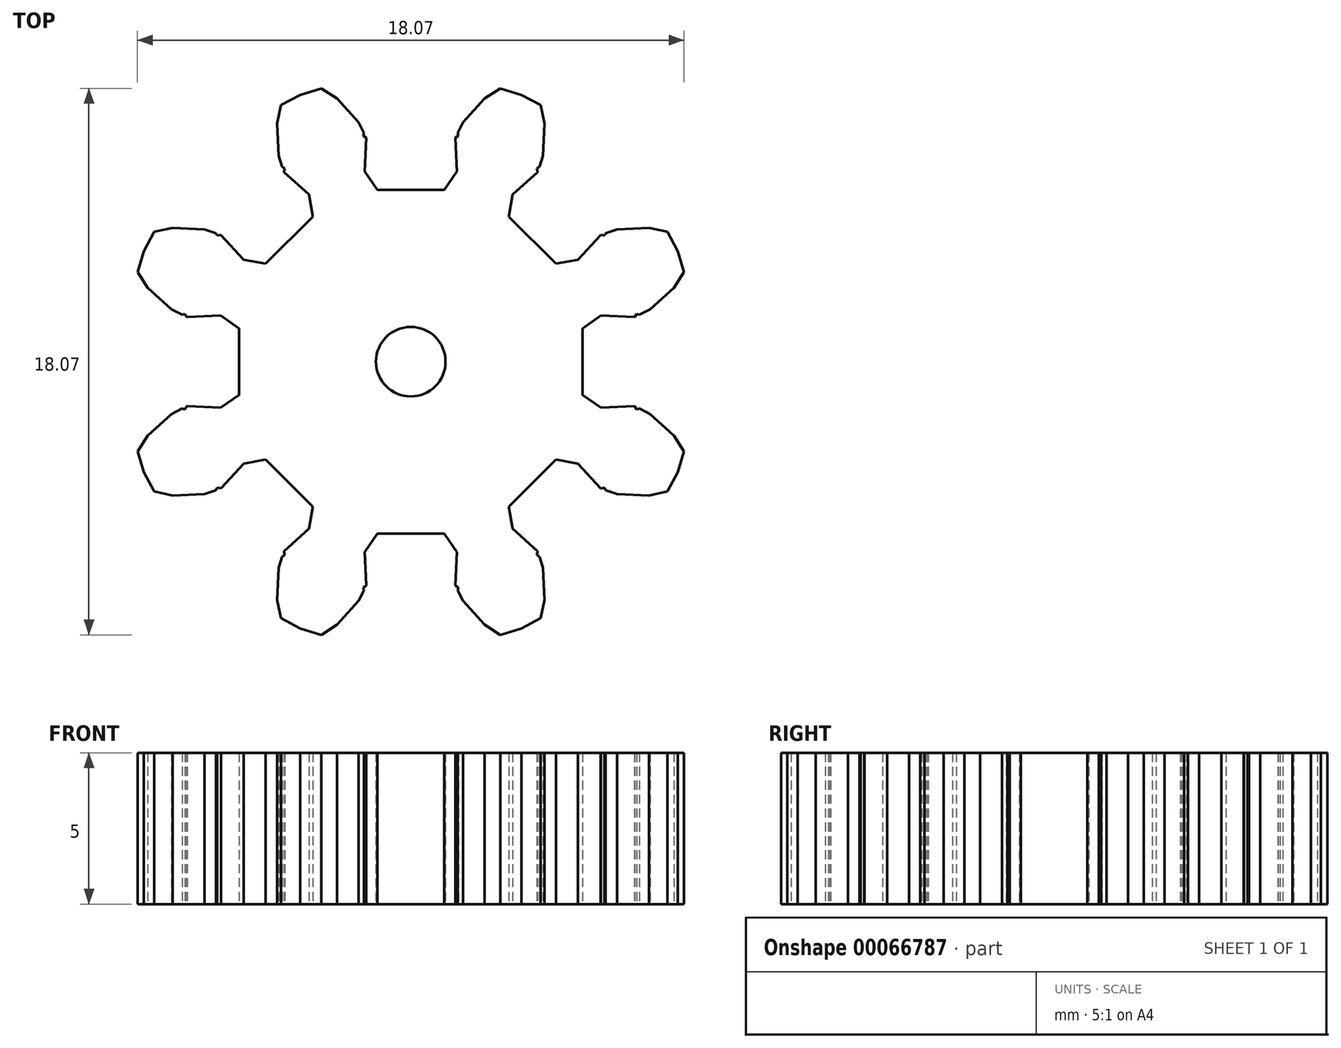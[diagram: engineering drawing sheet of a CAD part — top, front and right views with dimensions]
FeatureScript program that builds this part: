
annotation { "Feature Type Name" : "Feature", "Feature Type Description" : "" }
export const myFeature = defineFeature(function(context is Context, id is Id, definition is map)
    precondition{}
    {
        {
            var Q0;
            Q0=qCreatedBy(makeId("Top.planeOp"),FACE);
            var sketch = newSketch(context, id + "F0", { "sketchPlane" : qUnion([Q0])});
            skLineSegment(sketch, "E0", {"start": v(17.9, -7.29) * mm, "end": v(18.18, -6.43) * mm});
            skLineSegment(sketch, "E1", {"start": v(18.18, -6.43) * mm, "end": v(18.36, -5.54) * mm});
            skLineSegment(sketch, "E2", {"start": v(18.36, -5.54) * mm, "end": v(18.22, -5.43) * mm});
            skLineSegment(sketch, "E3", {"start": v(18.22, -5.43) * mm, "end": v(17.56, -4.97) * mm});
            skLineSegment(sketch, "E4", {"start": v(17.56, -4.97) * mm, "end": v(17, -4.65) * mm});
            skLineSegment(sketch, "E5", {"start": v(17, -4.65) * mm, "end": v(16.58, -4.46) * mm});
            skLineSegment(sketch, "E6", {"start": v(16.58, -4.46) * mm, "end": v(16.3, -4.36) * mm});
            skLineSegment(sketch, "E7", {"start": v(16.3, -4.36) * mm, "end": v(16.21, -4.33) * mm});
            skLineSegment(sketch, "E8", {"start": v(16.21, -4.33) * mm, "end": v(15.9, -4.3) * mm});
            skLineSegment(sketch, "E9", {"start": v(15.9, -4.3) * mm, "end": v(15.36, -4.19) * mm});
            skLineSegment(sketch, "E10", {"start": v(15.36, -4.19) * mm, "end": v(15, -4.02) * mm});
            skLineSegment(sketch, "E11", {"start": v(15, -4.02) * mm, "end": v(14.83, -3.83) * mm});
            skLineSegment(sketch, "E12", {"start": v(14.83, -3.83) * mm, "end": v(14.86, -3.66) * mm});
            skLineSegment(sketch, "E13", {"start": v(14.86, -3.66) * mm, "end": v(14.86, -3.65) * mm});
            skLineSegment(sketch, "E14", {"start": v(14.86, -3.65) * mm, "end": v(15.1, -1.83) * mm});
            skLineSegment(sketch, "E15", {"start": v(15.1, -1.83) * mm, "end": v(15.1, -1.82) * mm});
            skLineSegment(sketch, "E16", {"start": v(15.1, -1.82) * mm, "end": v(15.12, -1.65) * mm});
            skLineSegment(sketch, "E17", {"start": v(15.12, -1.65) * mm, "end": v(15.33, -1.51) * mm});
            skLineSegment(sketch, "E18", {"start": v(15.33, -1.51) * mm, "end": v(15.72, -1.44) * mm});
            skLineSegment(sketch, "E19", {"start": v(15.72, -1.44) * mm, "end": v(16.28, -1.46) * mm});
            skLineSegment(sketch, "E20", {"start": v(16.28, -1.46) * mm, "end": v(16.58, -1.52) * mm});
            skLineSegment(sketch, "E21", {"start": v(16.58, -1.52) * mm, "end": v(16.68, -1.52) * mm});
            skLineSegment(sketch, "E22", {"start": v(16.68, -1.52) * mm, "end": v(16.97, -1.5) * mm});
            skLineSegment(sketch, "E23", {"start": v(16.97, -1.5) * mm, "end": v(17.43, -1.42) * mm});
            skLineSegment(sketch, "E24", {"start": v(17.43, -1.42) * mm, "end": v(18.04, -1.26) * mm});
            skLineSegment(sketch, "E25", {"start": v(18.04, -1.26) * mm, "end": v(18.8, -0.98) * mm});
            skLineSegment(sketch, "E26", {"start": v(18.8, -0.98) * mm, "end": v(18.97, -0.9) * mm});
            skLineSegment(sketch, "E27", {"start": v(18.97, -0.9) * mm, "end": v(19.03, 0) * mm});
            skLineSegment(sketch, "E28", {"start": v(19.03, 0) * mm, "end": v(18.97, 0.9) * mm});
            skLineSegment(sketch, "E29", {"start": v(18.97, 0.9) * mm, "end": v(18.8, 0.98) * mm});
            skLineSegment(sketch, "E30", {"start": v(18.8, 0.98) * mm, "end": v(18.04, 1.25) * mm});
            skLineSegment(sketch, "E31", {"start": v(18.04, 1.25) * mm, "end": v(17.43, 1.4) * mm});
            skLineSegment(sketch, "E32", {"start": v(17.43, 1.4) * mm, "end": v(16.97, 1.49) * mm});
            skLineSegment(sketch, "E33", {"start": v(16.97, 1.49) * mm, "end": v(16.68, 1.51) * mm});
            skLineSegment(sketch, "E34", {"start": v(16.68, 1.51) * mm, "end": v(16.58, 1.51) * mm});
            skLineSegment(sketch, "E35", {"start": v(16.58, 1.51) * mm, "end": v(16.28, 1.46) * mm});
            skLineSegment(sketch, "E36", {"start": v(16.28, 1.46) * mm, "end": v(15.72, 1.43) * mm});
            skLineSegment(sketch, "E37", {"start": v(15.72, 1.43) * mm, "end": v(15.33, 1.5) * mm});
            skLineSegment(sketch, "E38", {"start": v(15.33, 1.5) * mm, "end": v(15.12, 1.64) * mm});
            skLineSegment(sketch, "E39", {"start": v(15.12, 1.64) * mm, "end": v(15.1, 1.8) * mm});
            skLineSegment(sketch, "E40", {"start": v(15.1, 1.8) * mm, "end": v(15.1, 1.82) * mm});
            skLineSegment(sketch, "E41", {"start": v(15.1, 1.82) * mm, "end": v(14.86, 3.64) * mm});
            skLineSegment(sketch, "E42", {"start": v(14.86, 3.64) * mm, "end": v(14.86, 3.65) * mm});
            skLineSegment(sketch, "E43", {"start": v(14.86, 3.65) * mm, "end": v(14.83, 3.82) * mm});
            skLineSegment(sketch, "E44", {"start": v(14.83, 3.82) * mm, "end": v(15, 4) * mm});
            skLineSegment(sketch, "E45", {"start": v(15, 4) * mm, "end": v(15.36, 4.18) * mm});
            skLineSegment(sketch, "E46", {"start": v(15.36, 4.18) * mm, "end": v(15.9, 4.3) * mm});
            skLineSegment(sketch, "E47", {"start": v(15.9, 4.3) * mm, "end": v(16.21, 4.33) * mm});
            skLineSegment(sketch, "E48", {"start": v(16.21, 4.33) * mm, "end": v(16.3, 4.35) * mm});
            skLineSegment(sketch, "E49", {"start": v(16.3, 4.35) * mm, "end": v(16.58, 4.45) * mm});
            skLineSegment(sketch, "E50", {"start": v(16.58, 4.45) * mm, "end": v(17, 4.64) * mm});
            skLineSegment(sketch, "E51", {"start": v(17, 4.64) * mm, "end": v(17.56, 4.96) * mm});
            skLineSegment(sketch, "E52", {"start": v(17.56, 4.96) * mm, "end": v(18.22, 5.42) * mm});
            skLineSegment(sketch, "E53", {"start": v(18.22, 5.42) * mm, "end": v(18.36, 5.53) * mm});
            skLineSegment(sketch, "E54", {"start": v(18.36, 5.53) * mm, "end": v(18.18, 6.42) * mm});
            skLineSegment(sketch, "E55", {"start": v(18.18, 6.42) * mm, "end": v(17.9, 7.28) * mm});
            skLineSegment(sketch, "E56", {"start": v(17.9, 7.28) * mm, "end": v(17.71, 7.31) * mm});
            skLineSegment(sketch, "E57", {"start": v(17.71, 7.31) * mm, "end": v(16.9, 7.38) * mm});
            skLineSegment(sketch, "E58", {"start": v(16.9, 7.38) * mm, "end": v(16.27, 7.37) * mm});
            skLineSegment(sketch, "E59", {"start": v(16.27, 7.37) * mm, "end": v(15.81, 7.33) * mm});
            skLineSegment(sketch, "E60", {"start": v(15.81, 7.33) * mm, "end": v(15.52, 7.28) * mm});
            skLineSegment(sketch, "E61", {"start": v(15.52, 7.28) * mm, "end": v(15.43, 7.25) * mm});
            skLineSegment(sketch, "E62", {"start": v(15.43, 7.25) * mm, "end": v(15.15, 7.12) * mm});
            skLineSegment(sketch, "E63", {"start": v(15.15, 7.12) * mm, "end": v(14.62, 6.95) * mm});
            skLineSegment(sketch, "E64", {"start": v(14.62, 6.95) * mm, "end": v(14.22, 6.92) * mm});
            skLineSegment(sketch, "E65", {"start": v(14.22, 6.92) * mm, "end": v(13.98, 7) * mm});
            skLineSegment(sketch, "E66", {"start": v(13.98, 7) * mm, "end": v(13.92, 7.16) * mm});
            skLineSegment(sketch, "E67", {"start": v(13.92, 7.16) * mm, "end": v(13.91, 7.17) * mm});
            skLineSegment(sketch, "E68", {"start": v(13.91, 7.17) * mm, "end": v(13.21, 8.86) * mm});
            skLineSegment(sketch, "E69", {"start": v(13.21, 8.86) * mm, "end": v(13.2, 8.88) * mm});
            skLineSegment(sketch, "E70", {"start": v(13.2, 8.88) * mm, "end": v(13.14, 9.03) * mm});
            skLineSegment(sketch, "E71", {"start": v(13.14, 9.03) * mm, "end": v(13.25, 9.26) * mm});
            skLineSegment(sketch, "E72", {"start": v(13.25, 9.26) * mm, "end": v(13.56, 9.51) * mm});
            skLineSegment(sketch, "E73", {"start": v(13.56, 9.51) * mm, "end": v(14.05, 9.77) * mm});
            skLineSegment(sketch, "E74", {"start": v(14.05, 9.77) * mm, "end": v(14.34, 9.88) * mm});
            skLineSegment(sketch, "E75", {"start": v(14.34, 9.88) * mm, "end": v(14.43, 9.92) * mm});
            skLineSegment(sketch, "E76", {"start": v(14.43, 9.92) * mm, "end": v(14.67, 10.1) * mm});
            skLineSegment(sketch, "E77", {"start": v(14.67, 10.1) * mm, "end": v(15.02, 10.39) * mm});
            skLineSegment(sketch, "E78", {"start": v(15.02, 10.39) * mm, "end": v(15.48, 10.83) * mm});
            skLineSegment(sketch, "E79", {"start": v(15.48, 10.83) * mm, "end": v(16, 11.45) * mm});
            skLineSegment(sketch, "E80", {"start": v(16, 11.45) * mm, "end": v(16.1, 11.6) * mm});
            skLineSegment(sketch, "E81", {"start": v(16.1, 11.6) * mm, "end": v(15.7, 12.41) * mm});
            skLineSegment(sketch, "E82", {"start": v(15.7, 12.41) * mm, "end": v(15.2, 13.16) * mm});
            skLineSegment(sketch, "E83", {"start": v(15.2, 13.16) * mm, "end": v(15.02, 13.15) * mm});
            skLineSegment(sketch, "E84", {"start": v(15.02, 13.15) * mm, "end": v(14.22, 13) * mm});
            skLineSegment(sketch, "E85", {"start": v(14.22, 13) * mm, "end": v(13.61, 12.84) * mm});
            skLineSegment(sketch, "E86", {"start": v(13.61, 12.84) * mm, "end": v(13.18, 12.67) * mm});
            skLineSegment(sketch, "E87", {"start": v(13.18, 12.67) * mm, "end": v(12.91, 12.55) * mm});
            skLineSegment(sketch, "E88", {"start": v(12.91, 12.55) * mm, "end": v(12.83, 12.5) * mm});
            skLineSegment(sketch, "E89", {"start": v(12.83, 12.5) * mm, "end": v(12.6, 12.3) * mm});
            skLineSegment(sketch, "E90", {"start": v(12.6, 12.3) * mm, "end": v(12.12, 12) * mm});
            skLineSegment(sketch, "E91", {"start": v(12.12, 12) * mm, "end": v(11.75, 11.87) * mm});
            skLineSegment(sketch, "E92", {"start": v(11.75, 11.87) * mm, "end": v(11.5, 11.88) * mm});
            skLineSegment(sketch, "E93", {"start": v(11.5, 11.88) * mm, "end": v(11.4, 12.01) * mm});
            skLineSegment(sketch, "E94", {"start": v(11.4, 12.01) * mm, "end": v(11.38, 12.03) * mm});
            skLineSegment(sketch, "E95", {"start": v(11.38, 12.03) * mm, "end": v(10.27, 13.48) * mm});
            skLineSegment(sketch, "E96", {"start": v(10.27, 13.48) * mm, "end": v(10.26, 13.5) * mm});
            skLineSegment(sketch, "E97", {"start": v(10.26, 13.5) * mm, "end": v(10.16, 13.63) * mm});
            skLineSegment(sketch, "E98", {"start": v(10.16, 13.63) * mm, "end": v(10.2, 13.87) * mm});
            skLineSegment(sketch, "E99", {"start": v(10.2, 13.87) * mm, "end": v(10.43, 14.2) * mm});
            skLineSegment(sketch, "E100", {"start": v(10.43, 14.2) * mm, "end": v(10.84, 14.58) * mm});
            skLineSegment(sketch, "E101", {"start": v(10.84, 14.58) * mm, "end": v(11.1, 14.75) * mm});
            skLineSegment(sketch, "E102", {"start": v(11.1, 14.75) * mm, "end": v(11.17, 14.82) * mm});
            skLineSegment(sketch, "E103", {"start": v(11.17, 14.82) * mm, "end": v(11.36, 15.05) * mm});
            skLineSegment(sketch, "E104", {"start": v(11.36, 15.05) * mm, "end": v(11.63, 15.42) * mm});
            skLineSegment(sketch, "E105", {"start": v(11.63, 15.42) * mm, "end": v(11.95, 15.97) * mm});
            skLineSegment(sketch, "E106", {"start": v(11.95, 15.97) * mm, "end": v(12.29, 16.7) * mm});
            skLineSegment(sketch, "E107", {"start": v(12.29, 16.7) * mm, "end": v(12.35, 16.87) * mm});
            skLineSegment(sketch, "E108", {"start": v(12.35, 16.87) * mm, "end": v(11.76, 17.55) * mm});
            skLineSegment(sketch, "E109", {"start": v(11.76, 17.55) * mm, "end": v(11.07, 18.15) * mm});
            skLineSegment(sketch, "E110", {"start": v(11.07, 18.15) * mm, "end": v(10.9, 18.09) * mm});
            skLineSegment(sketch, "E111", {"start": v(10.9, 18.09) * mm, "end": v(10.17, 17.74) * mm});
            skLineSegment(sketch, "E112", {"start": v(10.17, 17.74) * mm, "end": v(9.63, 17.42) * mm});
            skLineSegment(sketch, "E113", {"start": v(9.63, 17.42) * mm, "end": v(9.25, 17.15) * mm});
            skLineSegment(sketch, "E114", {"start": v(9.25, 17.15) * mm, "end": v(9.02, 16.96) * mm});
            skLineSegment(sketch, "E115", {"start": v(9.02, 16.96) * mm, "end": v(8.96, 16.9) * mm});
            skLineSegment(sketch, "E116", {"start": v(8.96, 16.9) * mm, "end": v(8.78, 16.64) * mm});
            skLineSegment(sketch, "E117", {"start": v(8.78, 16.64) * mm, "end": v(8.4, 16.23) * mm});
            skLineSegment(sketch, "E118", {"start": v(8.4, 16.23) * mm, "end": v(8.08, 16) * mm});
            skLineSegment(sketch, "E119", {"start": v(8.08, 16) * mm, "end": v(7.83, 15.95) * mm});
            skLineSegment(sketch, "E120", {"start": v(7.83, 15.95) * mm, "end": v(7.7, 16.06) * mm});
            skLineSegment(sketch, "E121", {"start": v(7.7, 16.06) * mm, "end": v(7.68, 16.07) * mm});
            skLineSegment(sketch, "E122", {"start": v(7.68, 16.07) * mm, "end": v(6.23, 17.18) * mm});
            skLineSegment(sketch, "E123", {"start": v(6.23, 17.18) * mm, "end": v(6.22, 17.19) * mm});
            skLineSegment(sketch, "E124", {"start": v(6.22, 17.19) * mm, "end": v(6.08, 17.3) * mm});
            skLineSegment(sketch, "E125", {"start": v(6.08, 17.3) * mm, "end": v(6.07, 17.54) * mm});
            skLineSegment(sketch, "E126", {"start": v(6.07, 17.54) * mm, "end": v(6.2, 17.92) * mm});
            skLineSegment(sketch, "E127", {"start": v(6.2, 17.92) * mm, "end": v(6.5, 18.39) * mm});
            skLineSegment(sketch, "E128", {"start": v(6.5, 18.39) * mm, "end": v(6.7, 18.62) * mm});
            skLineSegment(sketch, "E129", {"start": v(6.7, 18.62) * mm, "end": v(6.75, 18.7) * mm});
            skLineSegment(sketch, "E130", {"start": v(6.75, 18.7) * mm, "end": v(6.88, 18.97) * mm});
            skLineSegment(sketch, "E131", {"start": v(6.88, 18.97) * mm, "end": v(7.04, 19.4) * mm});
            skLineSegment(sketch, "E132", {"start": v(7.04, 19.4) * mm, "end": v(7.2, 20.02) * mm});
            skLineSegment(sketch, "E133", {"start": v(7.2, 20.02) * mm, "end": v(7.35, 20.81) * mm});
            skLineSegment(sketch, "E134", {"start": v(7.35, 20.81) * mm, "end": v(7.37, 21) * mm});
            skLineSegment(sketch, "E135", {"start": v(7.37, 21) * mm, "end": v(6.61, 21.5) * mm});
            skLineSegment(sketch, "E136", {"start": v(6.61, 21.5) * mm, "end": v(5.8, 21.9) * mm});
            skLineSegment(sketch, "E137", {"start": v(5.8, 21.9) * mm, "end": v(5.65, 21.8) * mm});
            skLineSegment(sketch, "E138", {"start": v(5.65, 21.8) * mm, "end": v(5.04, 21.27) * mm});
            skLineSegment(sketch, "E139", {"start": v(5.04, 21.27) * mm, "end": v(4.6, 20.82) * mm});
            skLineSegment(sketch, "E140", {"start": v(4.6, 20.82) * mm, "end": v(4.3, 20.46) * mm});
            skLineSegment(sketch, "E141", {"start": v(4.3, 20.46) * mm, "end": v(4.13, 20.22) * mm});
            skLineSegment(sketch, "E142", {"start": v(4.13, 20.22) * mm, "end": v(4.08, 20.14) * mm});
            skLineSegment(sketch, "E143", {"start": v(4.08, 20.14) * mm, "end": v(3.98, 19.85) * mm});
            skLineSegment(sketch, "E144", {"start": v(3.98, 19.85) * mm, "end": v(3.72, 19.35) * mm});
            skLineSegment(sketch, "E145", {"start": v(3.72, 19.35) * mm, "end": v(3.46, 19.05) * mm});
            skLineSegment(sketch, "E146", {"start": v(3.46, 19.05) * mm, "end": v(3.24, 18.94) * mm});
            skLineSegment(sketch, "E147", {"start": v(3.24, 18.94) * mm, "end": v(3.08, 19) * mm});
            skLineSegment(sketch, "E148", {"start": v(3.08, 19) * mm, "end": v(3.06, 19) * mm});
            skLineSegment(sketch, "E149", {"start": v(3.06, 19) * mm, "end": v(1.37, 19.7) * mm});
            skLineSegment(sketch, "E150", {"start": v(1.37, 19.7) * mm, "end": v(1.36, 19.71) * mm});
            skLineSegment(sketch, "E151", {"start": v(1.36, 19.71) * mm, "end": v(1.2, 19.78) * mm});
            skLineSegment(sketch, "E152", {"start": v(1.2, 19.78) * mm, "end": v(1.13, 20.02) * mm});
            skLineSegment(sketch, "E153", {"start": v(1.13, 20.02) * mm, "end": v(1.16, 20.41) * mm});
            skLineSegment(sketch, "E154", {"start": v(1.16, 20.41) * mm, "end": v(1.32, 20.95) * mm});
            skLineSegment(sketch, "E155", {"start": v(1.32, 20.95) * mm, "end": v(1.46, 21.23) * mm});
            skLineSegment(sketch, "E156", {"start": v(1.46, 21.23) * mm, "end": v(1.48, 21.32) * mm});
            skLineSegment(sketch, "E157", {"start": v(1.48, 21.32) * mm, "end": v(1.53, 21.6) * mm});
            skLineSegment(sketch, "E158", {"start": v(1.53, 21.6) * mm, "end": v(1.58, 22.07) * mm});
            skLineSegment(sketch, "E159", {"start": v(1.58, 22.07) * mm, "end": v(1.58, 22.7) * mm});
            skLineSegment(sketch, "E160", {"start": v(1.58, 22.7) * mm, "end": v(1.51, 23.5) * mm});
            skLineSegment(sketch, "E161", {"start": v(1.51, 23.5) * mm, "end": v(1.48, 23.69) * mm});
            skLineSegment(sketch, "E162", {"start": v(1.48, 23.69) * mm, "end": v(0.62, 23.98) * mm});
            skLineSegment(sketch, "E163", {"start": v(0.62, 23.98) * mm, "end": v(-0.26, 24.15) * mm});
            skLineSegment(sketch, "E164", {"start": v(-0.26, 24.15) * mm, "end": v(-0.38, 24.01) * mm});
            skLineSegment(sketch, "E165", {"start": v(-0.38, 24.01) * mm, "end": v(-0.84, 23.35) * mm});
            skLineSegment(sketch, "E166", {"start": v(-0.84, 23.35) * mm, "end": v(-1.15, 22.8) * mm});
            skLineSegment(sketch, "E167", {"start": v(-1.15, 22.8) * mm, "end": v(-1.35, 22.38) * mm});
            skLineSegment(sketch, "E168", {"start": v(-1.35, 22.38) * mm, "end": v(-1.45, 22.1) * mm});
            skLineSegment(sketch, "E169", {"start": v(-1.45, 22.1) * mm, "end": v(-1.47, 22) * mm});
            skLineSegment(sketch, "E170", {"start": v(-1.47, 22) * mm, "end": v(-1.5, 21.7) * mm});
            skLineSegment(sketch, "E171", {"start": v(-1.5, 21.7) * mm, "end": v(-1.62, 21.16) * mm});
            skLineSegment(sketch, "E172", {"start": v(-1.62, 21.16) * mm, "end": v(-1.79, 20.8) * mm});
            skLineSegment(sketch, "E173", {"start": v(-1.79, 20.8) * mm, "end": v(-1.97, 20.63) * mm});
            skLineSegment(sketch, "E174", {"start": v(-1.97, 20.63) * mm, "end": v(-2.14, 20.65) * mm});
            skLineSegment(sketch, "E175", {"start": v(-2.14, 20.65) * mm, "end": v(-2.16, 20.66) * mm});
            skLineSegment(sketch, "E176", {"start": v(-2.16, 20.66) * mm, "end": v(-3.97, 20.9) * mm});
            skLineSegment(sketch, "E177", {"start": v(-3.97, 20.9) * mm, "end": v(-3.99, 20.9) * mm});
            skLineSegment(sketch, "E178", {"start": v(-3.99, 20.9) * mm, "end": v(-4.16, 20.92) * mm});
            skLineSegment(sketch, "E179", {"start": v(-4.16, 20.92) * mm, "end": v(-4.3, 21.13) * mm});
            skLineSegment(sketch, "E180", {"start": v(-4.3, 21.13) * mm, "end": v(-4.36, 21.52) * mm});
            skLineSegment(sketch, "E181", {"start": v(-4.36, 21.52) * mm, "end": v(-4.34, 22.08) * mm});
            skLineSegment(sketch, "E182", {"start": v(-4.34, 22.08) * mm, "end": v(-4.29, 22.38) * mm});
            skLineSegment(sketch, "E183", {"start": v(-4.29, 22.38) * mm, "end": v(-4.29, 22.48) * mm});
            skLineSegment(sketch, "E184", {"start": v(-4.29, 22.48) * mm, "end": v(-4.3, 22.77) * mm});
            skLineSegment(sketch, "E185", {"start": v(-4.3, 22.77) * mm, "end": v(-4.39, 23.23) * mm});
            skLineSegment(sketch, "E186", {"start": v(-4.39, 23.23) * mm, "end": v(-4.55, 23.84) * mm});
            skLineSegment(sketch, "E187", {"start": v(-4.55, 23.84) * mm, "end": v(-4.82, 24.6) * mm});
            skLineSegment(sketch, "E188", {"start": v(-4.82, 24.6) * mm, "end": v(-4.9, 24.76) * mm});
            skLineSegment(sketch, "E189", {"start": v(-4.9, 24.76) * mm, "end": v(-5.8, 24.82) * mm});
            skLineSegment(sketch, "E190", {"start": v(-5.8, 24.82) * mm, "end": v(-6.7, 24.76) * mm});
            skLineSegment(sketch, "E191", {"start": v(-6.7, 24.76) * mm, "end": v(-6.78, 24.6) * mm});
            skLineSegment(sketch, "E192", {"start": v(-6.78, 24.6) * mm, "end": v(-7.05, 23.84) * mm});
            skLineSegment(sketch, "E193", {"start": v(-7.05, 23.84) * mm, "end": v(-7.21, 23.23) * mm});
            skLineSegment(sketch, "E194", {"start": v(-7.21, 23.23) * mm, "end": v(-7.3, 22.77) * mm});
            skLineSegment(sketch, "E195", {"start": v(-7.3, 22.77) * mm, "end": v(-7.32, 22.48) * mm});
            skLineSegment(sketch, "E196", {"start": v(-7.32, 22.48) * mm, "end": v(-7.32, 22.38) * mm});
            skLineSegment(sketch, "E197", {"start": v(-7.32, 22.38) * mm, "end": v(-7.26, 22.08) * mm});
            skLineSegment(sketch, "E198", {"start": v(-7.26, 22.08) * mm, "end": v(-7.24, 21.52) * mm});
            skLineSegment(sketch, "E199", {"start": v(-7.24, 21.52) * mm, "end": v(-7.3, 21.13) * mm});
            skLineSegment(sketch, "E200", {"start": v(-7.3, 21.13) * mm, "end": v(-7.44, 20.92) * mm});
            skLineSegment(sketch, "E201", {"start": v(-7.44, 20.92) * mm, "end": v(-7.61, 20.9) * mm});
            skLineSegment(sketch, "E202", {"start": v(-7.61, 20.9) * mm, "end": v(-7.63, 20.9) * mm});
            skLineSegment(sketch, "E203", {"start": v(-7.63, 20.9) * mm, "end": v(-9.44, 20.66) * mm});
            skLineSegment(sketch, "E204", {"start": v(-9.44, 20.66) * mm, "end": v(-9.46, 20.65) * mm});
            skLineSegment(sketch, "E205", {"start": v(-9.46, 20.65) * mm, "end": v(-9.63, 20.63) * mm});
            skLineSegment(sketch, "E206", {"start": v(-9.63, 20.63) * mm, "end": v(-9.81, 20.8) * mm});
            skLineSegment(sketch, "E207", {"start": v(-9.81, 20.8) * mm, "end": v(-9.98, 21.16) * mm});
            skLineSegment(sketch, "E208", {"start": v(-9.98, 21.16) * mm, "end": v(-10.1, 21.7) * mm});
            skLineSegment(sketch, "E209", {"start": v(-10.1, 21.7) * mm, "end": v(-10.13, 22) * mm});
            skLineSegment(sketch, "E210", {"start": v(-10.13, 22) * mm, "end": v(-10.16, 22.1) * mm});
            skLineSegment(sketch, "E211", {"start": v(-10.16, 22.1) * mm, "end": v(-10.26, 22.38) * mm});
            skLineSegment(sketch, "E212", {"start": v(-10.26, 22.38) * mm, "end": v(-10.45, 22.8) * mm});
            skLineSegment(sketch, "E213", {"start": v(-10.45, 22.8) * mm, "end": v(-10.76, 23.35) * mm});
            skLineSegment(sketch, "E214", {"start": v(-10.76, 23.35) * mm, "end": v(-11.22, 24.01) * mm});
            skLineSegment(sketch, "E215", {"start": v(-11.22, 24.01) * mm, "end": v(-11.34, 24.15) * mm});
            skLineSegment(sketch, "E216", {"start": v(-11.34, 24.15) * mm, "end": v(-12.23, 23.98) * mm});
            skLineSegment(sketch, "E217", {"start": v(-12.23, 23.98) * mm, "end": v(-13.08, 23.69) * mm});
            skLineSegment(sketch, "E218", {"start": v(-13.08, 23.69) * mm, "end": v(-13.12, 23.5) * mm});
            skLineSegment(sketch, "E219", {"start": v(-13.12, 23.5) * mm, "end": v(-13.18, 22.7) * mm});
            skLineSegment(sketch, "E220", {"start": v(-13.18, 22.7) * mm, "end": v(-13.18, 22.07) * mm});
            skLineSegment(sketch, "E221", {"start": v(-13.18, 22.07) * mm, "end": v(-13.14, 21.6) * mm});
            skLineSegment(sketch, "E222", {"start": v(-13.14, 21.6) * mm, "end": v(-13.08, 21.32) * mm});
            skLineSegment(sketch, "E223", {"start": v(-13.08, 21.32) * mm, "end": v(-13.06, 21.23) * mm});
            skLineSegment(sketch, "E224", {"start": v(-13.06, 21.23) * mm, "end": v(-12.93, 20.95) * mm});
            skLineSegment(sketch, "E225", {"start": v(-12.93, 20.95) * mm, "end": v(-12.76, 20.41) * mm});
            skLineSegment(sketch, "E226", {"start": v(-12.76, 20.41) * mm, "end": v(-12.73, 20.02) * mm});
            skLineSegment(sketch, "E227", {"start": v(-12.73, 20.02) * mm, "end": v(-12.8, 19.78) * mm});
            skLineSegment(sketch, "E228", {"start": v(-12.8, 19.78) * mm, "end": v(-12.96, 19.71) * mm});
            skLineSegment(sketch, "E229", {"start": v(-12.96, 19.71) * mm, "end": v(-12.98, 19.7) * mm});
            skLineSegment(sketch, "E230", {"start": v(-12.98, 19.7) * mm, "end": v(-14.67, 19) * mm});
            skLineSegment(sketch, "E231", {"start": v(-14.67, 19) * mm, "end": v(-14.68, 19) * mm});
            skLineSegment(sketch, "E232", {"start": v(-14.68, 19) * mm, "end": v(-14.84, 18.94) * mm});
            skLineSegment(sketch, "E233", {"start": v(-14.84, 18.94) * mm, "end": v(-15.06, 19.05) * mm});
            skLineSegment(sketch, "E234", {"start": v(-15.06, 19.05) * mm, "end": v(-15.32, 19.35) * mm});
            skLineSegment(sketch, "E235", {"start": v(-15.32, 19.35) * mm, "end": v(-15.58, 19.85) * mm});
            skLineSegment(sketch, "E236", {"start": v(-15.58, 19.85) * mm, "end": v(-15.68, 20.14) * mm});
            skLineSegment(sketch, "E237", {"start": v(-15.68, 20.14) * mm, "end": v(-15.73, 20.22) * mm});
            skLineSegment(sketch, "E238", {"start": v(-15.73, 20.22) * mm, "end": v(-15.9, 20.46) * mm});
            skLineSegment(sketch, "E239", {"start": v(-15.9, 20.46) * mm, "end": v(-16.2, 20.82) * mm});
            skLineSegment(sketch, "E240", {"start": v(-16.2, 20.82) * mm, "end": v(-16.64, 21.27) * mm});
            skLineSegment(sketch, "E241", {"start": v(-16.64, 21.27) * mm, "end": v(-17.25, 21.8) * mm});
            skLineSegment(sketch, "E242", {"start": v(-17.25, 21.8) * mm, "end": v(-17.4, 21.9) * mm});
            skLineSegment(sketch, "E243", {"start": v(-17.4, 21.9) * mm, "end": v(-18.22, 21.5) * mm});
            skLineSegment(sketch, "E244", {"start": v(-18.22, 21.5) * mm, "end": v(-18.97, 21) * mm});
            skLineSegment(sketch, "E245", {"start": v(-18.97, 21) * mm, "end": v(-18.95, 20.81) * mm});
            skLineSegment(sketch, "E246", {"start": v(-18.95, 20.81) * mm, "end": v(-18.8, 20.02) * mm});
            skLineSegment(sketch, "E247", {"start": v(-18.8, 20.02) * mm, "end": v(-18.64, 19.4) * mm});
            skLineSegment(sketch, "E248", {"start": v(-18.64, 19.4) * mm, "end": v(-18.48, 18.97) * mm});
            skLineSegment(sketch, "E249", {"start": v(-18.48, 18.97) * mm, "end": v(-18.35, 18.7) * mm});
            skLineSegment(sketch, "E250", {"start": v(-18.35, 18.7) * mm, "end": v(-18.3, 18.62) * mm});
            skLineSegment(sketch, "E251", {"start": v(-18.3, 18.62) * mm, "end": v(-18.1, 18.39) * mm});
            skLineSegment(sketch, "E252", {"start": v(-18.1, 18.39) * mm, "end": v(-17.8, 17.92) * mm});
            skLineSegment(sketch, "E253", {"start": v(-17.8, 17.92) * mm, "end": v(-17.67, 17.54) * mm});
            skLineSegment(sketch, "E254", {"start": v(-17.67, 17.54) * mm, "end": v(-17.69, 17.3) * mm});
            skLineSegment(sketch, "E255", {"start": v(-17.69, 17.3) * mm, "end": v(-17.82, 17.19) * mm});
            skLineSegment(sketch, "E256", {"start": v(-17.82, 17.19) * mm, "end": v(-17.83, 17.18) * mm});
            skLineSegment(sketch, "E257", {"start": v(-17.83, 17.18) * mm, "end": v(-19.29, 16.07) * mm});
            skLineSegment(sketch, "E258", {"start": v(-19.29, 16.07) * mm, "end": v(-19.3, 16.06) * mm});
            skLineSegment(sketch, "E259", {"start": v(-19.3, 16.06) * mm, "end": v(-19.43, 15.95) * mm});
            skLineSegment(sketch, "E260", {"start": v(-19.43, 15.95) * mm, "end": v(-19.68, 16) * mm});
            skLineSegment(sketch, "E261", {"start": v(-19.68, 16) * mm, "end": v(-20, 16.23) * mm});
            skLineSegment(sketch, "E262", {"start": v(-20, 16.23) * mm, "end": v(-20.38, 16.64) * mm});
            skLineSegment(sketch, "E263", {"start": v(-20.38, 16.64) * mm, "end": v(-20.56, 16.9) * mm});
            skLineSegment(sketch, "E264", {"start": v(-20.56, 16.9) * mm, "end": v(-20.63, 16.96) * mm});
            skLineSegment(sketch, "E265", {"start": v(-20.63, 16.96) * mm, "end": v(-20.85, 17.15) * mm});
            skLineSegment(sketch, "E266", {"start": v(-20.85, 17.15) * mm, "end": v(-21.23, 17.42) * mm});
            skLineSegment(sketch, "E267", {"start": v(-21.23, 17.42) * mm, "end": v(-21.78, 17.74) * mm});
            skLineSegment(sketch, "E268", {"start": v(-21.78, 17.74) * mm, "end": v(-22.5, 18.09) * mm});
            skLineSegment(sketch, "E269", {"start": v(-22.5, 18.09) * mm, "end": v(-22.68, 18.15) * mm});
            skLineSegment(sketch, "E270", {"start": v(-22.68, 18.15) * mm, "end": v(-23.36, 17.55) * mm});
            skLineSegment(sketch, "E271", {"start": v(-23.36, 17.55) * mm, "end": v(-23.95, 16.87) * mm});
            skLineSegment(sketch, "E272", {"start": v(-23.95, 16.87) * mm, "end": v(-23.9, 16.7) * mm});
            skLineSegment(sketch, "E273", {"start": v(-23.9, 16.7) * mm, "end": v(-23.55, 15.97) * mm});
            skLineSegment(sketch, "E274", {"start": v(-23.55, 15.97) * mm, "end": v(-23.23, 15.42) * mm});
            skLineSegment(sketch, "E275", {"start": v(-23.23, 15.42) * mm, "end": v(-22.96, 15.05) * mm});
            skLineSegment(sketch, "E276", {"start": v(-22.96, 15.05) * mm, "end": v(-22.77, 14.82) * mm});
            skLineSegment(sketch, "E277", {"start": v(-22.77, 14.82) * mm, "end": v(-22.7, 14.75) * mm});
            skLineSegment(sketch, "E278", {"start": v(-22.7, 14.75) * mm, "end": v(-22.45, 14.58) * mm});
            skLineSegment(sketch, "E279", {"start": v(-22.45, 14.58) * mm, "end": v(-22.04, 14.2) * mm});
            skLineSegment(sketch, "E280", {"start": v(-22.04, 14.2) * mm, "end": v(-21.81, 13.87) * mm});
            skLineSegment(sketch, "E281", {"start": v(-21.81, 13.87) * mm, "end": v(-21.76, 13.63) * mm});
            skLineSegment(sketch, "E282", {"start": v(-21.76, 13.63) * mm, "end": v(-21.86, 13.5) * mm});
            skLineSegment(sketch, "E283", {"start": v(-21.86, 13.5) * mm, "end": v(-21.87, 13.48) * mm});
            skLineSegment(sketch, "E284", {"start": v(-21.87, 13.48) * mm, "end": v(-22.99, 12.03) * mm});
            skLineSegment(sketch, "E285", {"start": v(-22.99, 12.03) * mm, "end": v(-23, 12.01) * mm});
            skLineSegment(sketch, "E286", {"start": v(-23, 12.01) * mm, "end": v(-23.1, 11.88) * mm});
            skLineSegment(sketch, "E287", {"start": v(-23.1, 11.88) * mm, "end": v(-23.35, 11.87) * mm});
            skLineSegment(sketch, "E288", {"start": v(-23.35, 11.87) * mm, "end": v(-23.72, 12) * mm});
            skLineSegment(sketch, "E289", {"start": v(-23.72, 12) * mm, "end": v(-24.2, 12.3) * mm});
            skLineSegment(sketch, "E290", {"start": v(-24.2, 12.3) * mm, "end": v(-24.43, 12.5) * mm});
            skLineSegment(sketch, "E291", {"start": v(-24.43, 12.5) * mm, "end": v(-24.51, 12.55) * mm});
            skLineSegment(sketch, "E292", {"start": v(-24.51, 12.55) * mm, "end": v(-24.78, 12.67) * mm});
            skLineSegment(sketch, "E293", {"start": v(-24.78, 12.67) * mm, "end": v(-25.21, 12.84) * mm});
            skLineSegment(sketch, "E294", {"start": v(-25.21, 12.84) * mm, "end": v(-25.83, 13) * mm});
            skLineSegment(sketch, "E295", {"start": v(-25.83, 13) * mm, "end": v(-26.62, 13.15) * mm});
            skLineSegment(sketch, "E296", {"start": v(-26.62, 13.15) * mm, "end": v(-26.8, 13.16) * mm});
            skLineSegment(sketch, "E297", {"start": v(-26.8, 13.16) * mm, "end": v(-27.3, 12.41) * mm});
            skLineSegment(sketch, "E298", {"start": v(-27.3, 12.41) * mm, "end": v(-27.7, 11.6) * mm});
            skLineSegment(sketch, "E299", {"start": v(-27.7, 11.6) * mm, "end": v(-27.6, 11.45) * mm});
            skLineSegment(sketch, "E300", {"start": v(-27.6, 11.45) * mm, "end": v(-27.08, 10.83) * mm});
            skLineSegment(sketch, "E301", {"start": v(-27.08, 10.83) * mm, "end": v(-26.63, 10.39) * mm});
            skLineSegment(sketch, "E302", {"start": v(-26.63, 10.39) * mm, "end": v(-26.27, 10.1) * mm});
            skLineSegment(sketch, "E303", {"start": v(-26.27, 10.1) * mm, "end": v(-26.03, 9.92) * mm});
            skLineSegment(sketch, "E304", {"start": v(-26.03, 9.92) * mm, "end": v(-25.94, 9.88) * mm});
            skLineSegment(sketch, "E305", {"start": v(-25.94, 9.88) * mm, "end": v(-25.65, 9.77) * mm});
            skLineSegment(sketch, "E306", {"start": v(-25.65, 9.77) * mm, "end": v(-25.16, 9.51) * mm});
            skLineSegment(sketch, "E307", {"start": v(-25.16, 9.51) * mm, "end": v(-24.86, 9.26) * mm});
            skLineSegment(sketch, "E308", {"start": v(-24.86, 9.26) * mm, "end": v(-24.74, 9.03) * mm});
            skLineSegment(sketch, "E309", {"start": v(-24.74, 9.03) * mm, "end": v(-24.8, 8.88) * mm});
            skLineSegment(sketch, "E310", {"start": v(-24.8, 8.88) * mm, "end": v(-24.81, 8.86) * mm});
            skLineSegment(sketch, "E311", {"start": v(-24.81, 8.86) * mm, "end": v(-25.51, 7.17) * mm});
            skLineSegment(sketch, "E312", {"start": v(-25.51, 7.17) * mm, "end": v(-25.52, 7.16) * mm});
            skLineSegment(sketch, "E313", {"start": v(-25.52, 7.16) * mm, "end": v(-25.59, 7) * mm});
            skLineSegment(sketch, "E314", {"start": v(-25.59, 7) * mm, "end": v(-25.82, 6.92) * mm});
            skLineSegment(sketch, "E315", {"start": v(-25.82, 6.92) * mm, "end": v(-26.22, 6.95) * mm});
            skLineSegment(sketch, "E316", {"start": v(-26.22, 6.95) * mm, "end": v(-26.75, 7.12) * mm});
            skLineSegment(sketch, "E317", {"start": v(-26.75, 7.12) * mm, "end": v(-27.03, 7.25) * mm});
            skLineSegment(sketch, "E318", {"start": v(-27.03, 7.25) * mm, "end": v(-27.12, 7.28) * mm});
            skLineSegment(sketch, "E319", {"start": v(-27.12, 7.28) * mm, "end": v(-27.41, 7.33) * mm});
            skLineSegment(sketch, "E320", {"start": v(-27.41, 7.33) * mm, "end": v(-27.88, 7.37) * mm});
            skLineSegment(sketch, "E321", {"start": v(-27.88, 7.37) * mm, "end": v(-28.5, 7.38) * mm});
            skLineSegment(sketch, "E322", {"start": v(-28.5, 7.38) * mm, "end": v(-29.31, 7.31) * mm});
            skLineSegment(sketch, "E323", {"start": v(-29.31, 7.31) * mm, "end": v(-29.5, 7.28) * mm});
            skLineSegment(sketch, "E324", {"start": v(-29.5, 7.28) * mm, "end": v(-29.78, 6.42) * mm});
            skLineSegment(sketch, "E325", {"start": v(-29.78, 6.42) * mm, "end": v(-29.96, 5.53) * mm});
            skLineSegment(sketch, "E326", {"start": v(-29.96, 5.53) * mm, "end": v(-29.82, 5.42) * mm});
            skLineSegment(sketch, "E327", {"start": v(-29.82, 5.42) * mm, "end": v(-29.16, 4.96) * mm});
            skLineSegment(sketch, "E328", {"start": v(-29.16, 4.96) * mm, "end": v(-28.6, 4.64) * mm});
            skLineSegment(sketch, "E329", {"start": v(-28.6, 4.64) * mm, "end": v(-28.19, 4.45) * mm});
            skLineSegment(sketch, "E330", {"start": v(-28.19, 4.45) * mm, "end": v(-27.9, 4.35) * mm});
            skLineSegment(sketch, "E331", {"start": v(-27.9, 4.35) * mm, "end": v(-27.81, 4.33) * mm});
            skLineSegment(sketch, "E332", {"start": v(-27.81, 4.33) * mm, "end": v(-27.5, 4.3) * mm});
            skLineSegment(sketch, "E333", {"start": v(-27.5, 4.3) * mm, "end": v(-26.96, 4.18) * mm});
            skLineSegment(sketch, "E334", {"start": v(-26.96, 4.18) * mm, "end": v(-26.6, 4) * mm});
            skLineSegment(sketch, "E335", {"start": v(-26.6, 4) * mm, "end": v(-26.44, 3.82) * mm});
            skLineSegment(sketch, "E336", {"start": v(-26.44, 3.82) * mm, "end": v(-26.46, 3.65) * mm});
            skLineSegment(sketch, "E337", {"start": v(-26.46, 3.65) * mm, "end": v(-26.46, 3.64) * mm});
            skLineSegment(sketch, "E338", {"start": v(-26.46, 3.64) * mm, "end": v(-26.7, 1.82) * mm});
            skLineSegment(sketch, "E339", {"start": v(-26.7, 1.82) * mm, "end": v(-26.7, 1.8) * mm});
            skLineSegment(sketch, "E340", {"start": v(-26.7, 1.8) * mm, "end": v(-26.72, 1.64) * mm});
            skLineSegment(sketch, "E341", {"start": v(-26.72, 1.64) * mm, "end": v(-26.93, 1.5) * mm});
            skLineSegment(sketch, "E342", {"start": v(-26.93, 1.5) * mm, "end": v(-27.32, 1.43) * mm});
            skLineSegment(sketch, "E343", {"start": v(-27.32, 1.43) * mm, "end": v(-27.88, 1.46) * mm});
            skLineSegment(sketch, "E344", {"start": v(-27.88, 1.46) * mm, "end": v(-28.18, 1.51) * mm});
            skLineSegment(sketch, "E345", {"start": v(-28.18, 1.51) * mm, "end": v(-28.28, 1.51) * mm});
            skLineSegment(sketch, "E346", {"start": v(-28.28, 1.51) * mm, "end": v(-28.58, 1.49) * mm});
            skLineSegment(sketch, "E347", {"start": v(-28.58, 1.49) * mm, "end": v(-29.03, 1.4) * mm});
            skLineSegment(sketch, "E348", {"start": v(-29.03, 1.4) * mm, "end": v(-29.65, 1.25) * mm});
            skLineSegment(sketch, "E349", {"start": v(-29.65, 1.25) * mm, "end": v(-30.4, 0.98) * mm});
            skLineSegment(sketch, "E350", {"start": v(-30.4, 0.98) * mm, "end": v(-30.57, 0.9) * mm});
            skLineSegment(sketch, "E351", {"start": v(-30.57, 0.9) * mm, "end": v(-30.63, 0) * mm});
            skLineSegment(sketch, "E352", {"start": v(-30.63, 0) * mm, "end": v(-30.57, -0.9) * mm});
            skLineSegment(sketch, "E353", {"start": v(-30.57, -0.9) * mm, "end": v(-30.4, -0.98) * mm});
            skLineSegment(sketch, "E354", {"start": v(-30.4, -0.98) * mm, "end": v(-29.65, -1.26) * mm});
            skLineSegment(sketch, "E355", {"start": v(-29.65, -1.26) * mm, "end": v(-29.03, -1.42) * mm});
            skLineSegment(sketch, "E356", {"start": v(-29.03, -1.42) * mm, "end": v(-28.58, -1.5) * mm});
            skLineSegment(sketch, "E357", {"start": v(-28.58, -1.5) * mm, "end": v(-28.28, -1.52) * mm});
            skLineSegment(sketch, "E358", {"start": v(-28.28, -1.52) * mm, "end": v(-28.18, -1.52) * mm});
            skLineSegment(sketch, "E359", {"start": v(-28.18, -1.52) * mm, "end": v(-27.88, -1.46) * mm});
            skLineSegment(sketch, "E360", {"start": v(-27.88, -1.46) * mm, "end": v(-27.32, -1.44) * mm});
            skLineSegment(sketch, "E361", {"start": v(-27.32, -1.44) * mm, "end": v(-26.93, -1.51) * mm});
            skLineSegment(sketch, "E362", {"start": v(-26.93, -1.51) * mm, "end": v(-26.72, -1.65) * mm});
            skLineSegment(sketch, "E363", {"start": v(-26.72, -1.65) * mm, "end": v(-26.7, -1.82) * mm});
            skLineSegment(sketch, "E364", {"start": v(-26.7, -1.82) * mm, "end": v(-26.7, -1.83) * mm});
            skLineSegment(sketch, "E365", {"start": v(-26.7, -1.83) * mm, "end": v(-26.46, -3.65) * mm});
            skLineSegment(sketch, "E366", {"start": v(-26.46, -3.65) * mm, "end": v(-26.46, -3.66) * mm});
            skLineSegment(sketch, "E367", {"start": v(-26.46, -3.66) * mm, "end": v(-26.44, -3.83) * mm});
            skLineSegment(sketch, "E368", {"start": v(-26.44, -3.83) * mm, "end": v(-26.6, -4.02) * mm});
            skLineSegment(sketch, "E369", {"start": v(-26.6, -4.02) * mm, "end": v(-26.96, -4.19) * mm});
            skLineSegment(sketch, "E370", {"start": v(-26.96, -4.19) * mm, "end": v(-27.5, -4.3) * mm});
            skLineSegment(sketch, "E371", {"start": v(-27.5, -4.3) * mm, "end": v(-27.81, -4.33) * mm});
            skLineSegment(sketch, "E372", {"start": v(-27.81, -4.33) * mm, "end": v(-27.9, -4.36) * mm});
            skLineSegment(sketch, "E373", {"start": v(-27.9, -4.36) * mm, "end": v(-28.19, -4.46) * mm});
            skLineSegment(sketch, "E374", {"start": v(-28.19, -4.46) * mm, "end": v(-28.6, -4.65) * mm});
            skLineSegment(sketch, "E375", {"start": v(-28.6, -4.65) * mm, "end": v(-29.16, -4.97) * mm});
            skLineSegment(sketch, "E376", {"start": v(-29.16, -4.97) * mm, "end": v(-29.82, -5.43) * mm});
            skLineSegment(sketch, "E377", {"start": v(-29.82, -5.43) * mm, "end": v(-29.96, -5.54) * mm});
            skLineSegment(sketch, "E378", {"start": v(-29.96, -5.54) * mm, "end": v(-29.78, -6.43) * mm});
            skLineSegment(sketch, "E379", {"start": v(-29.78, -6.43) * mm, "end": v(-29.5, -7.29) * mm});
            skLineSegment(sketch, "E380", {"start": v(-29.5, -7.29) * mm, "end": v(-29.31, -7.32) * mm});
            skLineSegment(sketch, "E381", {"start": v(-29.31, -7.32) * mm, "end": v(-28.5, -7.38) * mm});
            skLineSegment(sketch, "E382", {"start": v(-28.5, -7.38) * mm, "end": v(-27.88, -7.38) * mm});
            skLineSegment(sketch, "E383", {"start": v(-27.88, -7.38) * mm, "end": v(-27.41, -7.34) * mm});
            skLineSegment(sketch, "E384", {"start": v(-27.41, -7.34) * mm, "end": v(-27.12, -7.29) * mm});
            skLineSegment(sketch, "E385", {"start": v(-27.12, -7.29) * mm, "end": v(-27.03, -7.26) * mm});
            skLineSegment(sketch, "E386", {"start": v(-27.03, -7.26) * mm, "end": v(-26.75, -7.13) * mm});
            skLineSegment(sketch, "E387", {"start": v(-26.75, -7.13) * mm, "end": v(-26.22, -6.96) * mm});
            skLineSegment(sketch, "E388", {"start": v(-26.22, -6.96) * mm, "end": v(-25.82, -6.93) * mm});
            skLineSegment(sketch, "E389", {"start": v(-25.82, -6.93) * mm, "end": v(-25.59, -7) * mm});
            skLineSegment(sketch, "E390", {"start": v(-25.59, -7) * mm, "end": v(-25.52, -7.16) * mm});
            skLineSegment(sketch, "E391", {"start": v(-25.52, -7.16) * mm, "end": v(-25.51, -7.18) * mm});
            skLineSegment(sketch, "E392", {"start": v(-25.51, -7.18) * mm, "end": v(-24.81, -8.87) * mm});
            skLineSegment(sketch, "E393", {"start": v(-24.81, -8.87) * mm, "end": v(-24.8, -8.88) * mm});
            skLineSegment(sketch, "E394", {"start": v(-24.8, -8.88) * mm, "end": v(-24.74, -9.04) * mm});
            skLineSegment(sketch, "E395", {"start": v(-24.74, -9.04) * mm, "end": v(-24.86, -9.26) * mm});
            skLineSegment(sketch, "E396", {"start": v(-24.86, -9.26) * mm, "end": v(-25.16, -9.52) * mm});
            skLineSegment(sketch, "E397", {"start": v(-25.16, -9.52) * mm, "end": v(-25.65, -9.78) * mm});
            skLineSegment(sketch, "E398", {"start": v(-25.65, -9.78) * mm, "end": v(-25.94, -9.88) * mm});
            skLineSegment(sketch, "E399", {"start": v(-25.94, -9.88) * mm, "end": v(-26.03, -9.93) * mm});
            skLineSegment(sketch, "E400", {"start": v(-26.03, -9.93) * mm, "end": v(-26.27, -10.1) * mm});
            skLineSegment(sketch, "E401", {"start": v(-26.27, -10.1) * mm, "end": v(-26.63, -10.4) * mm});
            skLineSegment(sketch, "E402", {"start": v(-26.63, -10.4) * mm, "end": v(-27.08, -10.84) * mm});
            skLineSegment(sketch, "E403", {"start": v(-27.08, -10.84) * mm, "end": v(-27.6, -11.46) * mm});
            skLineSegment(sketch, "E404", {"start": v(-27.6, -11.46) * mm, "end": v(-27.7, -11.6) * mm});
            skLineSegment(sketch, "E405", {"start": v(-27.7, -11.6) * mm, "end": v(-27.3, -12.42) * mm});
            skLineSegment(sketch, "E406", {"start": v(-27.3, -12.42) * mm, "end": v(-26.8, -13.17) * mm});
            skLineSegment(sketch, "E407", {"start": v(-26.8, -13.17) * mm, "end": v(-26.62, -13.15) * mm});
            skLineSegment(sketch, "E408", {"start": v(-26.62, -13.15) * mm, "end": v(-25.83, -13.01) * mm});
            skLineSegment(sketch, "E409", {"start": v(-25.83, -13.01) * mm, "end": v(-25.21, -12.84) * mm});
            skLineSegment(sketch, "E410", {"start": v(-25.21, -12.84) * mm, "end": v(-24.78, -12.68) * mm});
            skLineSegment(sketch, "E411", {"start": v(-24.78, -12.68) * mm, "end": v(-24.51, -12.56) * mm});
            skLineSegment(sketch, "E412", {"start": v(-24.51, -12.56) * mm, "end": v(-24.43, -12.5) * mm});
            skLineSegment(sketch, "E413", {"start": v(-24.43, -12.5) * mm, "end": v(-24.2, -12.3) * mm});
            skLineSegment(sketch, "E414", {"start": v(-24.2, -12.3) * mm, "end": v(-23.72, -12) * mm});
            skLineSegment(sketch, "E415", {"start": v(-23.72, -12) * mm, "end": v(-23.35, -11.88) * mm});
            skLineSegment(sketch, "E416", {"start": v(-23.35, -11.88) * mm, "end": v(-23.1, -11.89) * mm});
            skLineSegment(sketch, "E417", {"start": v(-23.1, -11.89) * mm, "end": v(-23, -12.02) * mm});
            skLineSegment(sketch, "E418", {"start": v(-23, -12.02) * mm, "end": v(-22.99, -12.04) * mm});
            skLineSegment(sketch, "E419", {"start": v(-22.99, -12.04) * mm, "end": v(-21.87, -13.49) * mm});
            skLineSegment(sketch, "E420", {"start": v(-21.87, -13.49) * mm, "end": v(-21.86, -13.5) * mm});
            skLineSegment(sketch, "E421", {"start": v(-21.86, -13.5) * mm, "end": v(-21.76, -13.64) * mm});
            skLineSegment(sketch, "E422", {"start": v(-21.76, -13.64) * mm, "end": v(-21.81, -13.88) * mm});
            skLineSegment(sketch, "E423", {"start": v(-21.81, -13.88) * mm, "end": v(-22.04, -14.2) * mm});
            skLineSegment(sketch, "E424", {"start": v(-22.04, -14.2) * mm, "end": v(-22.45, -14.59) * mm});
            skLineSegment(sketch, "E425", {"start": v(-22.45, -14.59) * mm, "end": v(-22.7, -14.76) * mm});
            skLineSegment(sketch, "E426", {"start": v(-22.7, -14.76) * mm, "end": v(-22.77, -14.83) * mm});
            skLineSegment(sketch, "E427", {"start": v(-22.77, -14.83) * mm, "end": v(-22.96, -15.05) * mm});
            skLineSegment(sketch, "E428", {"start": v(-22.96, -15.05) * mm, "end": v(-23.23, -15.43) * mm});
            skLineSegment(sketch, "E429", {"start": v(-23.23, -15.43) * mm, "end": v(-23.55, -15.98) * mm});
            skLineSegment(sketch, "E430", {"start": v(-23.55, -15.98) * mm, "end": v(-23.9, -16.7) * mm});
            skLineSegment(sketch, "E431", {"start": v(-23.9, -16.7) * mm, "end": v(-23.95, -16.88) * mm});
            skLineSegment(sketch, "E432", {"start": v(-23.95, -16.88) * mm, "end": v(-23.36, -17.56) * mm});
            skLineSegment(sketch, "E433", {"start": v(-23.36, -17.56) * mm, "end": v(-22.68, -18.16) * mm});
            skLineSegment(sketch, "E434", {"start": v(-22.68, -18.16) * mm, "end": v(-22.5, -18.1) * mm});
            skLineSegment(sketch, "E435", {"start": v(-22.5, -18.1) * mm, "end": v(-21.78, -17.75) * mm});
            skLineSegment(sketch, "E436", {"start": v(-21.78, -17.75) * mm, "end": v(-21.23, -17.43) * mm});
            skLineSegment(sketch, "E437", {"start": v(-21.23, -17.43) * mm, "end": v(-20.85, -17.16) * mm});
            skLineSegment(sketch, "E438", {"start": v(-20.85, -17.16) * mm, "end": v(-20.63, -16.97) * mm});
            skLineSegment(sketch, "E439", {"start": v(-20.63, -16.97) * mm, "end": v(-20.56, -16.9) * mm});
            skLineSegment(sketch, "E440", {"start": v(-20.56, -16.9) * mm, "end": v(-20.38, -16.65) * mm});
            skLineSegment(sketch, "E441", {"start": v(-20.38, -16.65) * mm, "end": v(-20, -16.24) * mm});
            skLineSegment(sketch, "E442", {"start": v(-20, -16.24) * mm, "end": v(-19.68, -16.01) * mm});
            skLineSegment(sketch, "E443", {"start": v(-19.68, -16.01) * mm, "end": v(-19.43, -15.96) * mm});
            skLineSegment(sketch, "E444", {"start": v(-19.43, -15.96) * mm, "end": v(-19.3, -16.06) * mm});
            skLineSegment(sketch, "E445", {"start": v(-19.3, -16.06) * mm, "end": v(-19.29, -16.07) * mm});
            skLineSegment(sketch, "E446", {"start": v(-19.29, -16.07) * mm, "end": v(-17.83, -17.19) * mm});
            skLineSegment(sketch, "E447", {"start": v(-17.83, -17.19) * mm, "end": v(-17.82, -17.2) * mm});
            skLineSegment(sketch, "E448", {"start": v(-17.82, -17.2) * mm, "end": v(-17.69, -17.3) * mm});
            skLineSegment(sketch, "E449", {"start": v(-17.69, -17.3) * mm, "end": v(-17.67, -17.55) * mm});
            skLineSegment(sketch, "E450", {"start": v(-17.67, -17.55) * mm, "end": v(-17.8, -17.92) * mm});
            skLineSegment(sketch, "E451", {"start": v(-17.8, -17.92) * mm, "end": v(-18.1, -18.4) * mm});
            skLineSegment(sketch, "E452", {"start": v(-18.1, -18.4) * mm, "end": v(-18.3, -18.63) * mm});
            skLineSegment(sketch, "E453", {"start": v(-18.3, -18.63) * mm, "end": v(-18.35, -18.72) * mm});
            skLineSegment(sketch, "E454", {"start": v(-18.35, -18.72) * mm, "end": v(-18.48, -18.98) * mm});
            skLineSegment(sketch, "E455", {"start": v(-18.48, -18.98) * mm, "end": v(-18.64, -19.42) * mm});
            skLineSegment(sketch, "E456", {"start": v(-18.64, -19.42) * mm, "end": v(-18.8, -20.03) * mm});
            skLineSegment(sketch, "E457", {"start": v(-18.8, -20.03) * mm, "end": v(-18.95, -20.82) * mm});
            skLineSegment(sketch, "E458", {"start": v(-18.95, -20.82) * mm, "end": v(-18.97, -21) * mm});
            skLineSegment(sketch, "E459", {"start": v(-18.97, -21) * mm, "end": v(-18.22, -21.5) * mm});
            skLineSegment(sketch, "E460", {"start": v(-18.22, -21.5) * mm, "end": v(-17.4, -21.9) * mm});
            skLineSegment(sketch, "E461", {"start": v(-17.4, -21.9) * mm, "end": v(-17.25, -21.8) * mm});
            skLineSegment(sketch, "E462", {"start": v(-17.25, -21.8) * mm, "end": v(-16.64, -21.28) * mm});
            skLineSegment(sketch, "E463", {"start": v(-16.64, -21.28) * mm, "end": v(-16.2, -20.83) * mm});
            skLineSegment(sketch, "E464", {"start": v(-16.2, -20.83) * mm, "end": v(-15.9, -20.47) * mm});
            skLineSegment(sketch, "E465", {"start": v(-15.9, -20.47) * mm, "end": v(-15.73, -20.23) * mm});
            skLineSegment(sketch, "E466", {"start": v(-15.73, -20.23) * mm, "end": v(-15.68, -20.15) * mm});
            skLineSegment(sketch, "E467", {"start": v(-15.68, -20.15) * mm, "end": v(-15.58, -19.86) * mm});
            skLineSegment(sketch, "E468", {"start": v(-15.58, -19.86) * mm, "end": v(-15.32, -19.36) * mm});
            skLineSegment(sketch, "E469", {"start": v(-15.32, -19.36) * mm, "end": v(-15.06, -19.06) * mm});
            skLineSegment(sketch, "E470", {"start": v(-15.06, -19.06) * mm, "end": v(-14.84, -18.95) * mm});
            skLineSegment(sketch, "E471", {"start": v(-14.84, -18.95) * mm, "end": v(-14.68, -19) * mm});
            skLineSegment(sketch, "E472", {"start": v(-14.68, -19) * mm, "end": v(-14.67, -19.02) * mm});
            skLineSegment(sketch, "E473", {"start": v(-14.67, -19.02) * mm, "end": v(-12.98, -19.72) * mm});
            skLineSegment(sketch, "E474", {"start": v(-12.98, -19.72) * mm, "end": v(-12.96, -19.72) * mm});
            skLineSegment(sketch, "E475", {"start": v(-12.96, -19.72) * mm, "end": v(-12.8, -19.79) * mm});
            skLineSegment(sketch, "E476", {"start": v(-12.8, -19.79) * mm, "end": v(-12.73, -20.03) * mm});
            skLineSegment(sketch, "E477", {"start": v(-12.73, -20.03) * mm, "end": v(-12.76, -20.42) * mm});
            skLineSegment(sketch, "E478", {"start": v(-12.76, -20.42) * mm, "end": v(-12.93, -20.95) * mm});
            skLineSegment(sketch, "E479", {"start": v(-12.93, -20.95) * mm, "end": v(-13.06, -21.23) * mm});
            skLineSegment(sketch, "E480", {"start": v(-13.06, -21.23) * mm, "end": v(-13.08, -21.33) * mm});
            skLineSegment(sketch, "E481", {"start": v(-13.08, -21.33) * mm, "end": v(-13.14, -21.62) * mm});
            skLineSegment(sketch, "E482", {"start": v(-13.14, -21.62) * mm, "end": v(-13.18, -22.08) * mm});
            skLineSegment(sketch, "E483", {"start": v(-13.18, -22.08) * mm, "end": v(-13.18, -22.71) * mm});
            skLineSegment(sketch, "E484", {"start": v(-13.18, -22.71) * mm, "end": v(-13.12, -23.52) * mm});
            skLineSegment(sketch, "E485", {"start": v(-13.12, -23.52) * mm, "end": v(-13.08, -23.7) * mm});
            skLineSegment(sketch, "E486", {"start": v(-13.08, -23.7) * mm, "end": v(-12.23, -23.99) * mm});
            skLineSegment(sketch, "E487", {"start": v(-12.23, -23.99) * mm, "end": v(-11.34, -24.16) * mm});
            skLineSegment(sketch, "E488", {"start": v(-11.34, -24.16) * mm, "end": v(-11.22, -24.02) * mm});
            skLineSegment(sketch, "E489", {"start": v(-11.22, -24.02) * mm, "end": v(-10.76, -23.36) * mm});
            skLineSegment(sketch, "E490", {"start": v(-10.76, -23.36) * mm, "end": v(-10.45, -22.8) * mm});
            skLineSegment(sketch, "E491", {"start": v(-10.45, -22.8) * mm, "end": v(-10.26, -22.39) * mm});
            skLineSegment(sketch, "E492", {"start": v(-10.26, -22.39) * mm, "end": v(-10.16, -22.11) * mm});
            skLineSegment(sketch, "E493", {"start": v(-10.16, -22.11) * mm, "end": v(-10.13, -22.02) * mm});
            skLineSegment(sketch, "E494", {"start": v(-10.13, -22.02) * mm, "end": v(-10.1, -21.71) * mm});
            skLineSegment(sketch, "E495", {"start": v(-10.1, -21.71) * mm, "end": v(-9.98, -21.17) * mm});
            skLineSegment(sketch, "E496", {"start": v(-9.98, -21.17) * mm, "end": v(-9.81, -20.8) * mm});
            skLineSegment(sketch, "E497", {"start": v(-9.81, -20.8) * mm, "end": v(-9.63, -20.64) * mm});
            skLineSegment(sketch, "E498", {"start": v(-9.63, -20.64) * mm, "end": v(-9.46, -20.66) * mm});
            skLineSegment(sketch, "E499", {"start": v(-9.46, -20.66) * mm, "end": v(-9.44, -20.66) * mm});
            skLineSegment(sketch, "E500", {"start": v(-9.44, -20.66) * mm, "end": v(-7.63, -20.9) * mm});
            skLineSegment(sketch, "E501", {"start": v(-7.63, -20.9) * mm, "end": v(-7.61, -20.9) * mm});
            skLineSegment(sketch, "E502", {"start": v(-7.61, -20.9) * mm, "end": v(-7.44, -20.93) * mm});
            skLineSegment(sketch, "E503", {"start": v(-7.44, -20.93) * mm, "end": v(-7.3, -21.14) * mm});
            skLineSegment(sketch, "E504", {"start": v(-7.3, -21.14) * mm, "end": v(-7.24, -21.53) * mm});
            skLineSegment(sketch, "E505", {"start": v(-7.24, -21.53) * mm, "end": v(-7.26, -22.08) * mm});
            skLineSegment(sketch, "E506", {"start": v(-7.26, -22.08) * mm, "end": v(-7.32, -22.39) * mm});
            skLineSegment(sketch, "E507", {"start": v(-7.32, -22.39) * mm, "end": v(-7.32, -22.49) * mm});
            skLineSegment(sketch, "E508", {"start": v(-7.32, -22.49) * mm, "end": v(-7.3, -22.78) * mm});
            skLineSegment(sketch, "E509", {"start": v(-7.3, -22.78) * mm, "end": v(-7.21, -23.24) * mm});
            skLineSegment(sketch, "E510", {"start": v(-7.21, -23.24) * mm, "end": v(-7.05, -23.85) * mm});
            skLineSegment(sketch, "E511", {"start": v(-7.05, -23.85) * mm, "end": v(-6.78, -24.6) * mm});
            skLineSegment(sketch, "E512", {"start": v(-6.78, -24.6) * mm, "end": v(-6.7, -24.77) * mm});
            skLineSegment(sketch, "E513", {"start": v(-6.7, -24.77) * mm, "end": v(-5.8, -24.83) * mm});
            skLineSegment(sketch, "E514", {"start": v(-5.8, -24.83) * mm, "end": v(-4.9, -24.77) * mm});
            skLineSegment(sketch, "E515", {"start": v(-4.9, -24.77) * mm, "end": v(-4.82, -24.6) * mm});
            skLineSegment(sketch, "E516", {"start": v(-4.82, -24.6) * mm, "end": v(-4.55, -23.85) * mm});
            skLineSegment(sketch, "E517", {"start": v(-4.55, -23.85) * mm, "end": v(-4.39, -23.24) * mm});
            skLineSegment(sketch, "E518", {"start": v(-4.39, -23.24) * mm, "end": v(-4.3, -22.78) * mm});
            skLineSegment(sketch, "E519", {"start": v(-4.3, -22.78) * mm, "end": v(-4.29, -22.49) * mm});
            skLineSegment(sketch, "E520", {"start": v(-4.29, -22.49) * mm, "end": v(-4.29, -22.39) * mm});
            skLineSegment(sketch, "E521", {"start": v(-4.29, -22.39) * mm, "end": v(-4.34, -22.08) * mm});
            skLineSegment(sketch, "E522", {"start": v(-4.34, -22.08) * mm, "end": v(-4.36, -21.53) * mm});
            skLineSegment(sketch, "E523", {"start": v(-4.36, -21.53) * mm, "end": v(-4.3, -21.14) * mm});
            skLineSegment(sketch, "E524", {"start": v(-4.3, -21.14) * mm, "end": v(-4.16, -20.93) * mm});
            skLineSegment(sketch, "E525", {"start": v(-4.16, -20.93) * mm, "end": v(-3.99, -20.9) * mm});
            skLineSegment(sketch, "E526", {"start": v(-3.99, -20.9) * mm, "end": v(-3.97, -20.9) * mm});
            skLineSegment(sketch, "E527", {"start": v(-3.97, -20.9) * mm, "end": v(-2.16, -20.66) * mm});
            skLineSegment(sketch, "E528", {"start": v(-2.16, -20.66) * mm, "end": v(-2.14, -20.66) * mm});
            skLineSegment(sketch, "E529", {"start": v(-2.14, -20.66) * mm, "end": v(-1.97, -20.64) * mm});
            skLineSegment(sketch, "E530", {"start": v(-1.97, -20.64) * mm, "end": v(-1.79, -20.8) * mm});
            skLineSegment(sketch, "E531", {"start": v(-1.79, -20.8) * mm, "end": v(-1.62, -21.17) * mm});
            skLineSegment(sketch, "E532", {"start": v(-1.62, -21.17) * mm, "end": v(-1.5, -21.71) * mm});
            skLineSegment(sketch, "E533", {"start": v(-1.5, -21.71) * mm, "end": v(-1.47, -22.02) * mm});
            skLineSegment(sketch, "E534", {"start": v(-1.47, -22.02) * mm, "end": v(-1.45, -22.11) * mm});
            skLineSegment(sketch, "E535", {"start": v(-1.45, -22.11) * mm, "end": v(-1.35, -22.39) * mm});
            skLineSegment(sketch, "E536", {"start": v(-1.35, -22.39) * mm, "end": v(-1.15, -22.8) * mm});
            skLineSegment(sketch, "E537", {"start": v(-1.15, -22.8) * mm, "end": v(-0.84, -23.36) * mm});
            skLineSegment(sketch, "E538", {"start": v(-0.84, -23.36) * mm, "end": v(-0.38, -24.02) * mm});
            skLineSegment(sketch, "E539", {"start": v(-0.38, -24.02) * mm, "end": v(-0.26, -24.16) * mm});
            skLineSegment(sketch, "E540", {"start": v(-0.26, -24.16) * mm, "end": v(0.62, -23.99) * mm});
            skLineSegment(sketch, "E541", {"start": v(0.62, -23.99) * mm, "end": v(1.48, -23.7) * mm});
            skLineSegment(sketch, "E542", {"start": v(1.48, -23.7) * mm, "end": v(1.51, -23.52) * mm});
            skLineSegment(sketch, "E543", {"start": v(1.51, -23.52) * mm, "end": v(1.58, -22.71) * mm});
            skLineSegment(sketch, "E544", {"start": v(1.58, -22.71) * mm, "end": v(1.58, -22.08) * mm});
            skLineSegment(sketch, "E545", {"start": v(1.58, -22.08) * mm, "end": v(1.53, -21.62) * mm});
            skLineSegment(sketch, "E546", {"start": v(1.53, -21.62) * mm, "end": v(1.48, -21.33) * mm});
            skLineSegment(sketch, "E547", {"start": v(1.48, -21.33) * mm, "end": v(1.46, -21.23) * mm});
            skLineSegment(sketch, "E548", {"start": v(1.46, -21.23) * mm, "end": v(1.32, -20.95) * mm});
            skLineSegment(sketch, "E549", {"start": v(1.32, -20.95) * mm, "end": v(1.16, -20.42) * mm});
            skLineSegment(sketch, "E550", {"start": v(1.16, -20.42) * mm, "end": v(1.13, -20.03) * mm});
            skLineSegment(sketch, "E551", {"start": v(1.13, -20.03) * mm, "end": v(1.2, -19.79) * mm});
            skLineSegment(sketch, "E552", {"start": v(1.2, -19.79) * mm, "end": v(1.36, -19.72) * mm});
            skLineSegment(sketch, "E553", {"start": v(1.36, -19.72) * mm, "end": v(1.37, -19.72) * mm});
            skLineSegment(sketch, "E554", {"start": v(1.37, -19.72) * mm, "end": v(3.06, -19.02) * mm});
            skLineSegment(sketch, "E555", {"start": v(3.06, -19.02) * mm, "end": v(3.08, -19) * mm});
            skLineSegment(sketch, "E556", {"start": v(3.08, -19) * mm, "end": v(3.24, -18.95) * mm});
            skLineSegment(sketch, "E557", {"start": v(3.24, -18.95) * mm, "end": v(3.46, -19.06) * mm});
            skLineSegment(sketch, "E558", {"start": v(3.46, -19.06) * mm, "end": v(3.72, -19.36) * mm});
            skLineSegment(sketch, "E559", {"start": v(3.72, -19.36) * mm, "end": v(3.98, -19.86) * mm});
            skLineSegment(sketch, "E560", {"start": v(3.98, -19.86) * mm, "end": v(4.08, -20.15) * mm});
            skLineSegment(sketch, "E561", {"start": v(4.08, -20.15) * mm, "end": v(4.13, -20.23) * mm});
            skLineSegment(sketch, "E562", {"start": v(4.13, -20.23) * mm, "end": v(4.3, -20.47) * mm});
            skLineSegment(sketch, "E563", {"start": v(4.3, -20.47) * mm, "end": v(4.6, -20.83) * mm});
            skLineSegment(sketch, "E564", {"start": v(4.6, -20.83) * mm, "end": v(5.04, -21.28) * mm});
            skLineSegment(sketch, "E565", {"start": v(5.04, -21.28) * mm, "end": v(5.65, -21.8) * mm});
            skLineSegment(sketch, "E566", {"start": v(5.65, -21.8) * mm, "end": v(5.8, -21.9) * mm});
            skLineSegment(sketch, "E567", {"start": v(5.8, -21.9) * mm, "end": v(6.61, -21.5) * mm});
            skLineSegment(sketch, "E568", {"start": v(6.61, -21.5) * mm, "end": v(7.37, -21) * mm});
            skLineSegment(sketch, "E569", {"start": v(7.37, -21) * mm, "end": v(7.35, -20.82) * mm});
            skLineSegment(sketch, "E570", {"start": v(7.35, -20.82) * mm, "end": v(7.2, -20.03) * mm});
            skLineSegment(sketch, "E571", {"start": v(7.2, -20.03) * mm, "end": v(7.04, -19.42) * mm});
            skLineSegment(sketch, "E572", {"start": v(7.04, -19.42) * mm, "end": v(6.88, -18.98) * mm});
            skLineSegment(sketch, "E573", {"start": v(6.88, -18.98) * mm, "end": v(6.75, -18.72) * mm});
            skLineSegment(sketch, "E574", {"start": v(6.75, -18.72) * mm, "end": v(6.7, -18.63) * mm});
            skLineSegment(sketch, "E575", {"start": v(6.7, -18.63) * mm, "end": v(6.5, -18.4) * mm});
            skLineSegment(sketch, "E576", {"start": v(6.5, -18.4) * mm, "end": v(6.2, -17.92) * mm});
            skLineSegment(sketch, "E577", {"start": v(6.2, -17.92) * mm, "end": v(6.07, -17.55) * mm});
            skLineSegment(sketch, "E578", {"start": v(6.07, -17.55) * mm, "end": v(6.08, -17.3) * mm});
            skLineSegment(sketch, "E579", {"start": v(6.08, -17.3) * mm, "end": v(6.22, -17.2) * mm});
            skLineSegment(sketch, "E580", {"start": v(6.22, -17.2) * mm, "end": v(6.23, -17.19) * mm});
            skLineSegment(sketch, "E581", {"start": v(6.23, -17.19) * mm, "end": v(7.68, -16.07) * mm});
            skLineSegment(sketch, "E582", {"start": v(7.68, -16.07) * mm, "end": v(7.7, -16.06) * mm});
            skLineSegment(sketch, "E583", {"start": v(7.7, -16.06) * mm, "end": v(7.83, -15.96) * mm});
            skLineSegment(sketch, "E584", {"start": v(7.83, -15.96) * mm, "end": v(8.08, -16.01) * mm});
            skLineSegment(sketch, "E585", {"start": v(8.08, -16.01) * mm, "end": v(8.4, -16.24) * mm});
            skLineSegment(sketch, "E586", {"start": v(8.4, -16.24) * mm, "end": v(8.78, -16.65) * mm});
            skLineSegment(sketch, "E587", {"start": v(8.78, -16.65) * mm, "end": v(8.96, -16.9) * mm});
            skLineSegment(sketch, "E588", {"start": v(8.96, -16.9) * mm, "end": v(9.02, -16.97) * mm});
            skLineSegment(sketch, "E589", {"start": v(9.02, -16.97) * mm, "end": v(9.25, -17.16) * mm});
            skLineSegment(sketch, "E590", {"start": v(9.25, -17.16) * mm, "end": v(9.63, -17.43) * mm});
            skLineSegment(sketch, "E591", {"start": v(9.63, -17.43) * mm, "end": v(10.17, -17.75) * mm});
            skLineSegment(sketch, "E592", {"start": v(10.17, -17.75) * mm, "end": v(10.9, -18.1) * mm});
            skLineSegment(sketch, "E593", {"start": v(10.9, -18.1) * mm, "end": v(11.07, -18.16) * mm});
            skLineSegment(sketch, "E594", {"start": v(11.07, -18.16) * mm, "end": v(11.76, -17.56) * mm});
            skLineSegment(sketch, "E595", {"start": v(11.76, -17.56) * mm, "end": v(12.35, -16.88) * mm});
            skLineSegment(sketch, "E596", {"start": v(12.35, -16.88) * mm, "end": v(12.29, -16.7) * mm});
            skLineSegment(sketch, "E597", {"start": v(12.29, -16.7) * mm, "end": v(11.95, -15.98) * mm});
            skLineSegment(sketch, "E598", {"start": v(11.95, -15.98) * mm, "end": v(11.63, -15.43) * mm});
            skLineSegment(sketch, "E599", {"start": v(11.63, -15.43) * mm, "end": v(11.36, -15.05) * mm});
            skLineSegment(sketch, "E600", {"start": v(11.36, -15.05) * mm, "end": v(11.17, -14.83) * mm});
            skLineSegment(sketch, "E601", {"start": v(11.17, -14.83) * mm, "end": v(11.1, -14.76) * mm});
            skLineSegment(sketch, "E602", {"start": v(11.1, -14.76) * mm, "end": v(10.84, -14.59) * mm});
            skLineSegment(sketch, "E603", {"start": v(10.84, -14.59) * mm, "end": v(10.43, -14.2) * mm});
            skLineSegment(sketch, "E604", {"start": v(10.43, -14.2) * mm, "end": v(10.2, -13.88) * mm});
            skLineSegment(sketch, "E605", {"start": v(10.2, -13.88) * mm, "end": v(10.16, -13.64) * mm});
            skLineSegment(sketch, "E606", {"start": v(10.16, -13.64) * mm, "end": v(10.26, -13.5) * mm});
            skLineSegment(sketch, "E607", {"start": v(10.26, -13.5) * mm, "end": v(10.27, -13.49) * mm});
            skLineSegment(sketch, "E608", {"start": v(10.27, -13.49) * mm, "end": v(11.38, -12.04) * mm});
            skLineSegment(sketch, "E609", {"start": v(11.38, -12.04) * mm, "end": v(11.4, -12.02) * mm});
            skLineSegment(sketch, "E610", {"start": v(11.4, -12.02) * mm, "end": v(11.5, -11.89) * mm});
            skLineSegment(sketch, "E611", {"start": v(11.5, -11.89) * mm, "end": v(11.75, -11.88) * mm});
            skLineSegment(sketch, "E612", {"start": v(11.75, -11.88) * mm, "end": v(12.12, -12) * mm});
            skLineSegment(sketch, "E613", {"start": v(12.12, -12) * mm, "end": v(12.6, -12.3) * mm});
            skLineSegment(sketch, "E614", {"start": v(12.6, -12.3) * mm, "end": v(12.83, -12.5) * mm});
            skLineSegment(sketch, "E615", {"start": v(12.83, -12.5) * mm, "end": v(12.91, -12.56) * mm});
            skLineSegment(sketch, "E616", {"start": v(12.91, -12.56) * mm, "end": v(13.18, -12.68) * mm});
            skLineSegment(sketch, "E617", {"start": v(13.18, -12.68) * mm, "end": v(13.61, -12.84) * mm});
            skLineSegment(sketch, "E618", {"start": v(13.61, -12.84) * mm, "end": v(14.22, -13.01) * mm});
            skLineSegment(sketch, "E619", {"start": v(14.22, -13.01) * mm, "end": v(15.02, -13.15) * mm});
            skLineSegment(sketch, "E620", {"start": v(15.02, -13.15) * mm, "end": v(15.2, -13.17) * mm});
            skLineSegment(sketch, "E621", {"start": v(15.2, -13.17) * mm, "end": v(15.7, -12.42) * mm});
            skLineSegment(sketch, "E622", {"start": v(15.7, -12.42) * mm, "end": v(16.1, -11.6) * mm});
            skLineSegment(sketch, "E623", {"start": v(16.1, -11.6) * mm, "end": v(16, -11.46) * mm});
            skLineSegment(sketch, "E624", {"start": v(16, -11.46) * mm, "end": v(15.48, -10.84) * mm});
            skLineSegment(sketch, "E625", {"start": v(15.48, -10.84) * mm, "end": v(15.02, -10.4) * mm});
            skLineSegment(sketch, "E626", {"start": v(15.02, -10.4) * mm, "end": v(14.67, -10.1) * mm});
            skLineSegment(sketch, "E627", {"start": v(14.67, -10.1) * mm, "end": v(14.43, -9.93) * mm});
            skLineSegment(sketch, "E628", {"start": v(14.43, -9.93) * mm, "end": v(14.34, -9.88) * mm});
            skLineSegment(sketch, "E629", {"start": v(14.34, -9.88) * mm, "end": v(14.05, -9.78) * mm});
            skLineSegment(sketch, "E630", {"start": v(14.05, -9.78) * mm, "end": v(13.56, -9.52) * mm});
            skLineSegment(sketch, "E631", {"start": v(13.56, -9.52) * mm, "end": v(13.25, -9.26) * mm});
            skLineSegment(sketch, "E632", {"start": v(13.25, -9.26) * mm, "end": v(13.14, -9.04) * mm});
            skLineSegment(sketch, "E633", {"start": v(13.14, -9.04) * mm, "end": v(13.2, -8.88) * mm});
            skLineSegment(sketch, "E634", {"start": v(13.2, -8.88) * mm, "end": v(13.21, -8.87) * mm});
            skLineSegment(sketch, "E635", {"start": v(13.21, -8.87) * mm, "end": v(13.91, -7.18) * mm});
            skLineSegment(sketch, "E636", {"start": v(13.91, -7.18) * mm, "end": v(13.92, -7.16) * mm});
            skLineSegment(sketch, "E637", {"start": v(13.92, -7.16) * mm, "end": v(13.98, -7) * mm});
            skLineSegment(sketch, "E638", {"start": v(13.98, -7) * mm, "end": v(14.22, -6.93) * mm});
            skLineSegment(sketch, "E639", {"start": v(14.22, -6.93) * mm, "end": v(14.62, -6.96) * mm});
            skLineSegment(sketch, "E640", {"start": v(14.62, -6.96) * mm, "end": v(15.15, -7.13) * mm});
            skLineSegment(sketch, "E641", {"start": v(15.15, -7.13) * mm, "end": v(15.43, -7.26) * mm});
            skLineSegment(sketch, "E642", {"start": v(15.43, -7.26) * mm, "end": v(15.52, -7.29) * mm});
            skLineSegment(sketch, "E643", {"start": v(15.52, -7.29) * mm, "end": v(15.81, -7.34) * mm});
            skLineSegment(sketch, "E644", {"start": v(15.81, -7.34) * mm, "end": v(16.27, -7.38) * mm});
            skLineSegment(sketch, "E645", {"start": v(16.27, -7.38) * mm, "end": v(16.9, -7.38) * mm});
            skLineSegment(sketch, "E646", {"start": v(16.9, -7.38) * mm, "end": v(17.71, -7.32) * mm});
            skLineSegment(sketch, "E647", {"start": v(17.71, -7.32) * mm, "end": v(17.9, -7.29) * mm});
            skLineSegment(sketch, "E648", {"start": v(16.28, 4.29) * mm, "end": v(15.93, 3.65) * mm});
            skLineSegment(sketch, "E649", {"start": v(15.93, 3.65) * mm, "end": v(15.72, 2.96) * mm});
            skLineSegment(sketch, "E650", {"start": v(15.72, 2.96) * mm, "end": v(16.06, 2.44) * mm});
            skLineSegment(sketch, "E651", {"start": v(16.06, 2.44) * mm, "end": v(16.85, 1.73) * mm});
            skLineSegment(sketch, "E652", {"start": v(16.85, 1.73) * mm, "end": v(17.2, 1.55) * mm});
            skLineSegment(sketch, "E653", {"start": v(17.2, 1.55) * mm, "end": v(17.29, 1.57) * mm});
            skLineSegment(sketch, "E654", {"start": v(17.29, 1.57) * mm, "end": v(17.35, 1.47) * mm});
            skLineSegment(sketch, "E655", {"start": v(17.35, 1.47) * mm, "end": v(17.36, 1.47) * mm});
            skLineSegment(sketch, "E656", {"start": v(17.36, 1.47) * mm, "end": v(18.47, 1.52) * mm});
            skLineSegment(sketch, "E657", {"start": v(18.47, 1.52) * mm, "end": v(19.08, 1.1) * mm});
            skLineSegment(sketch, "E658", {"start": v(19.08, 1.1) * mm, "end": v(19.08, -1.1) * mm});
            skLineSegment(sketch, "E659", {"start": v(19.08, -1.1) * mm, "end": v(18.47, -1.53) * mm});
            skLineSegment(sketch, "E660", {"start": v(18.47, -1.53) * mm, "end": v(17.36, -1.48) * mm});
            skLineSegment(sketch, "E661", {"start": v(17.36, -1.48) * mm, "end": v(17.35, -1.48) * mm});
            skLineSegment(sketch, "E662", {"start": v(17.35, -1.48) * mm, "end": v(17.29, -1.58) * mm});
            skLineSegment(sketch, "E663", {"start": v(17.29, -1.58) * mm, "end": v(17.2, -1.55) * mm});
            skLineSegment(sketch, "E664", {"start": v(17.2, -1.55) * mm, "end": v(16.85, -1.73) * mm});
            skLineSegment(sketch, "E665", {"start": v(16.85, -1.73) * mm, "end": v(16.06, -2.45) * mm});
            skLineSegment(sketch, "E666", {"start": v(16.06, -2.45) * mm, "end": v(15.72, -2.97) * mm});
            skLineSegment(sketch, "E667", {"start": v(15.72, -2.97) * mm, "end": v(15.93, -3.66) * mm});
            skLineSegment(sketch, "E668", {"start": v(15.93, -3.66) * mm, "end": v(16.28, -4.3) * mm});
            skLineSegment(sketch, "E669", {"start": v(16.28, -4.3) * mm, "end": v(16.88, -4.43) * mm});
            skLineSegment(sketch, "E670", {"start": v(16.88, -4.43) * mm, "end": v(17.94, -4.38) * mm});
            skLineSegment(sketch, "E671", {"start": v(17.94, -4.38) * mm, "end": v(18.32, -4.25) * mm});
            skLineSegment(sketch, "E672", {"start": v(18.32, -4.25) * mm, "end": v(18.36, -4.17) * mm});
            skLineSegment(sketch, "E673", {"start": v(18.47, -4.2) * mm, "end": v(18.49, -4.2) * mm});
            skLineSegment(sketch, "E674", {"start": v(18.49, -4.2) * mm, "end": v(19.23, -3.37) * mm});
            skLineSegment(sketch, "E675", {"start": v(19.23, -3.37) * mm, "end": v(19.96, -3.24) * mm});
            skLineSegment(sketch, "E676", {"start": v(19.96, -3.24) * mm, "end": v(21.52, -4.8) * mm});
            skLineSegment(sketch, "E677", {"start": v(21.52, -4.8) * mm, "end": v(21.39, -5.53) * mm});
            skLineSegment(sketch, "E678", {"start": v(21.39, -5.53) * mm, "end": v(20.57, -6.27) * mm});
            skLineSegment(sketch, "E679", {"start": v(20.57, -6.27) * mm, "end": v(20.56, -6.29) * mm});
            skLineSegment(sketch, "E680", {"start": v(20.56, -6.29) * mm, "end": v(20.6, -6.4) * mm});
            skLineSegment(sketch, "E681", {"start": v(20.6, -6.4) * mm, "end": v(20.5, -6.45) * mm});
            skLineSegment(sketch, "E682", {"start": v(20.5, -6.45) * mm, "end": v(20.39, -6.82) * mm});
            skLineSegment(sketch, "E683", {"start": v(20.39, -6.82) * mm, "end": v(20.33, -7.88) * mm});
            skLineSegment(sketch, "E684", {"start": v(20.33, -7.88) * mm, "end": v(20.46, -8.49) * mm});
            skLineSegment(sketch, "E685", {"start": v(20.46, -8.49) * mm, "end": v(21.1, -8.83) * mm});
            skLineSegment(sketch, "E686", {"start": v(21.1, -8.83) * mm, "end": v(21.8, -9.04) * mm});
            skLineSegment(sketch, "E687", {"start": v(21.8, -9.04) * mm, "end": v(22.31, -8.7) * mm});
            skLineSegment(sketch, "E688", {"start": v(22.31, -8.7) * mm, "end": v(23.03, -7.92) * mm});
            skLineSegment(sketch, "E689", {"start": v(23.03, -7.92) * mm, "end": v(23.2, -7.56) * mm});
            skLineSegment(sketch, "E690", {"start": v(23.2, -7.56) * mm, "end": v(23.18, -7.47) * mm});
            skLineSegment(sketch, "E691", {"start": v(23.18, -7.47) * mm, "end": v(23.28, -7.41) * mm});
            skLineSegment(sketch, "E692", {"start": v(23.28, -7.41) * mm, "end": v(23.28, -7.4) * mm});
            skLineSegment(sketch, "E693", {"start": v(23.28, -7.4) * mm, "end": v(23.23, -6.3) * mm});
            skLineSegment(sketch, "E694", {"start": v(23.23, -6.3) * mm, "end": v(23.66, -5.68) * mm});
            skLineSegment(sketch, "E695", {"start": v(23.66, -5.68) * mm, "end": v(25.86, -5.68) * mm});
            skLineSegment(sketch, "E696", {"start": v(25.86, -5.68) * mm, "end": v(26.28, -6.3) * mm});
            skLineSegment(sketch, "E697", {"start": v(26.28, -6.3) * mm, "end": v(26.23, -7.4) * mm});
            skLineSegment(sketch, "E698", {"start": v(26.23, -7.4) * mm, "end": v(26.23, -7.41) * mm});
            skLineSegment(sketch, "E699", {"start": v(26.23, -7.41) * mm, "end": v(26.33, -7.47) * mm});
            skLineSegment(sketch, "E700", {"start": v(26.33, -7.47) * mm, "end": v(26.3, -7.56) * mm});
            skLineSegment(sketch, "E701", {"start": v(26.3, -7.56) * mm, "end": v(26.49, -7.92) * mm});
            skLineSegment(sketch, "E702", {"start": v(26.49, -7.92) * mm, "end": v(27.2, -8.7) * mm});
            skLineSegment(sketch, "E703", {"start": v(27.2, -8.7) * mm, "end": v(27.72, -9.04) * mm});
            skLineSegment(sketch, "E704", {"start": v(27.72, -9.04) * mm, "end": v(28.41, -8.83) * mm});
            skLineSegment(sketch, "E705", {"start": v(28.41, -8.83) * mm, "end": v(29.05, -8.49) * mm});
            skLineSegment(sketch, "E706", {"start": v(29.05, -8.49) * mm, "end": v(29.18, -7.88) * mm});
            skLineSegment(sketch, "E707", {"start": v(29.18, -7.88) * mm, "end": v(29.13, -6.82) * mm});
            skLineSegment(sketch, "E708", {"start": v(29.13, -6.82) * mm, "end": v(29, -6.45) * mm});
            skLineSegment(sketch, "E709", {"start": v(29, -6.45) * mm, "end": v(28.92, -6.4) * mm});
            skLineSegment(sketch, "E710", {"start": v(28.92, -6.4) * mm, "end": v(28.95, -6.29) * mm});
            skLineSegment(sketch, "E711", {"start": v(28.95, -6.29) * mm, "end": v(28.94, -6.27) * mm});
            skLineSegment(sketch, "E712", {"start": v(28.94, -6.27) * mm, "end": v(28.12, -5.53) * mm});
            skLineSegment(sketch, "E713", {"start": v(28.12, -5.53) * mm, "end": v(28, -4.8) * mm});
            skLineSegment(sketch, "E714", {"start": v(28, -4.8) * mm, "end": v(29.55, -3.24) * mm});
            skLineSegment(sketch, "E715", {"start": v(29.55, -3.24) * mm, "end": v(30.28, -3.37) * mm});
            skLineSegment(sketch, "E716", {"start": v(30.28, -3.37) * mm, "end": v(31.02, -4.2) * mm});
            skLineSegment(sketch, "E717", {"start": v(31.02, -4.2) * mm, "end": v(31.04, -4.2) * mm});
            skLineSegment(sketch, "E718", {"start": v(31.04, -4.2) * mm, "end": v(31.15, -4.17) * mm});
            skLineSegment(sketch, "E719", {"start": v(31.15, -4.17) * mm, "end": v(31.2, -4.25) * mm});
            skLineSegment(sketch, "E720", {"start": v(31.2, -4.25) * mm, "end": v(31.57, -4.38) * mm});
            skLineSegment(sketch, "E721", {"start": v(31.57, -4.38) * mm, "end": v(32.63, -4.43) * mm});
            skLineSegment(sketch, "E722", {"start": v(32.63, -4.43) * mm, "end": v(33.24, -4.3) * mm});
            skLineSegment(sketch, "E723", {"start": v(33.24, -4.3) * mm, "end": v(33.58, -3.66) * mm});
            skLineSegment(sketch, "E724", {"start": v(33.58, -3.66) * mm, "end": v(33.79, -2.97) * mm});
            skLineSegment(sketch, "E725", {"start": v(33.79, -2.97) * mm, "end": v(33.45, -2.45) * mm});
            skLineSegment(sketch, "E726", {"start": v(33.45, -2.45) * mm, "end": v(32.67, -1.73) * mm});
            skLineSegment(sketch, "E727", {"start": v(32.67, -1.73) * mm, "end": v(32.32, -1.55) * mm});
            skLineSegment(sketch, "E728", {"start": v(32.32, -1.55) * mm, "end": v(32.23, -1.58) * mm});
            skLineSegment(sketch, "E729", {"start": v(32.23, -1.58) * mm, "end": v(32.17, -1.48) * mm});
            skLineSegment(sketch, "E730", {"start": v(32.17, -1.48) * mm, "end": v(32.15, -1.48) * mm});
            skLineSegment(sketch, "E731", {"start": v(32.15, -1.48) * mm, "end": v(31.05, -1.53) * mm});
            skLineSegment(sketch, "E732", {"start": v(31.05, -1.53) * mm, "end": v(30.44, -1.1) * mm});
            skLineSegment(sketch, "E733", {"start": v(30.44, -1.1) * mm, "end": v(30.44, 1.1) * mm});
            skLineSegment(sketch, "E734", {"start": v(30.44, 1.1) * mm, "end": v(31.05, 1.52) * mm});
            skLineSegment(sketch, "E735", {"start": v(31.05, 1.52) * mm, "end": v(32.15, 1.47) * mm});
            skLineSegment(sketch, "E736", {"start": v(32.15, 1.47) * mm, "end": v(32.17, 1.47) * mm});
            skLineSegment(sketch, "E737", {"start": v(32.17, 1.47) * mm, "end": v(32.23, 1.57) * mm});
            skLineSegment(sketch, "E738", {"start": v(32.23, 1.57) * mm, "end": v(32.32, 1.55) * mm});
            skLineSegment(sketch, "E739", {"start": v(32.32, 1.55) * mm, "end": v(32.67, 1.73) * mm});
            skLineSegment(sketch, "E740", {"start": v(32.67, 1.73) * mm, "end": v(33.45, 2.44) * mm});
            skLineSegment(sketch, "E741", {"start": v(33.45, 2.44) * mm, "end": v(33.79, 2.96) * mm});
            skLineSegment(sketch, "E742", {"start": v(33.79, 2.96) * mm, "end": v(33.58, 3.65) * mm});
            skLineSegment(sketch, "E743", {"start": v(33.58, 3.65) * mm, "end": v(33.24, 4.29) * mm});
            skLineSegment(sketch, "E744", {"start": v(33.24, 4.29) * mm, "end": v(32.63, 4.42) * mm});
            skLineSegment(sketch, "E745", {"start": v(32.63, 4.42) * mm, "end": v(31.57, 4.37) * mm});
            skLineSegment(sketch, "E746", {"start": v(31.57, 4.37) * mm, "end": v(31.2, 4.25) * mm});
            skLineSegment(sketch, "E747", {"start": v(31.2, 4.25) * mm, "end": v(31.15, 4.16) * mm});
            skLineSegment(sketch, "E748", {"start": v(31.15, 4.16) * mm, "end": v(31.04, 4.2) * mm});
            skLineSegment(sketch, "E749", {"start": v(31.04, 4.2) * mm, "end": v(31.02, 4.18) * mm});
            skLineSegment(sketch, "E750", {"start": v(31.02, 4.18) * mm, "end": v(30.28, 3.36) * mm});
            skLineSegment(sketch, "E751", {"start": v(30.28, 3.36) * mm, "end": v(29.55, 3.23) * mm});
            skLineSegment(sketch, "E752", {"start": v(29.55, 3.23) * mm, "end": v(28, 4.8) * mm});
            skLineSegment(sketch, "E753", {"start": v(28, 4.8) * mm, "end": v(28.12, 5.52) * mm});
            skLineSegment(sketch, "E754", {"start": v(28.12, 5.52) * mm, "end": v(28.94, 6.26) * mm});
            skLineSegment(sketch, "E755", {"start": v(28.94, 6.26) * mm, "end": v(28.95, 6.28) * mm});
            skLineSegment(sketch, "E756", {"start": v(28.95, 6.28) * mm, "end": v(28.92, 6.4) * mm});
            skLineSegment(sketch, "E757", {"start": v(28.92, 6.4) * mm, "end": v(29, 6.44) * mm});
            skLineSegment(sketch, "E758", {"start": v(29, 6.44) * mm, "end": v(29.13, 6.81) * mm});
            skLineSegment(sketch, "E759", {"start": v(29.13, 6.81) * mm, "end": v(29.18, 7.87) * mm});
            skLineSegment(sketch, "E760", {"start": v(29.18, 7.87) * mm, "end": v(29.05, 8.48) * mm});
            skLineSegment(sketch, "E761", {"start": v(29.05, 8.48) * mm, "end": v(28.41, 8.82) * mm});
            skLineSegment(sketch, "E762", {"start": v(28.41, 8.82) * mm, "end": v(27.72, 9.03) * mm});
            skLineSegment(sketch, "E763", {"start": v(27.72, 9.03) * mm, "end": v(27.2, 8.7) * mm});
            skLineSegment(sketch, "E764", {"start": v(27.2, 8.7) * mm, "end": v(26.49, 7.9) * mm});
            skLineSegment(sketch, "E765", {"start": v(26.49, 7.9) * mm, "end": v(26.3, 7.56) * mm});
            skLineSegment(sketch, "E766", {"start": v(26.3, 7.56) * mm, "end": v(26.33, 7.47) * mm});
            skLineSegment(sketch, "E767", {"start": v(26.33, 7.47) * mm, "end": v(26.23, 7.4) * mm});
            skLineSegment(sketch, "E768", {"start": v(26.23, 7.4) * mm, "end": v(26.23, 7.39) * mm});
            skLineSegment(sketch, "E769", {"start": v(26.23, 7.39) * mm, "end": v(26.28, 6.28) * mm});
            skLineSegment(sketch, "E770", {"start": v(26.28, 6.28) * mm, "end": v(25.86, 5.68) * mm});
            skLineSegment(sketch, "E771", {"start": v(25.86, 5.68) * mm, "end": v(23.66, 5.68) * mm});
            skLineSegment(sketch, "E772", {"start": v(23.66, 5.68) * mm, "end": v(23.23, 6.28) * mm});
            skLineSegment(sketch, "E773", {"start": v(23.23, 6.28) * mm, "end": v(23.28, 7.39) * mm});
            skLineSegment(sketch, "E774", {"start": v(23.28, 7.39) * mm, "end": v(23.28, 7.4) * mm});
            skLineSegment(sketch, "E775", {"start": v(23.28, 7.4) * mm, "end": v(23.18, 7.47) * mm});
            skLineSegment(sketch, "E776", {"start": v(23.18, 7.47) * mm, "end": v(23.2, 7.56) * mm});
            skLineSegment(sketch, "E777", {"start": v(23.2, 7.56) * mm, "end": v(23.03, 7.9) * mm});
            skLineSegment(sketch, "E778", {"start": v(23.03, 7.9) * mm, "end": v(22.31, 8.7) * mm});
            skLineSegment(sketch, "E779", {"start": v(22.31, 8.7) * mm, "end": v(21.8, 9.03) * mm});
            skLineSegment(sketch, "E780", {"start": v(21.8, 9.03) * mm, "end": v(21.1, 8.82) * mm});
            skLineSegment(sketch, "E781", {"start": v(21.1, 8.82) * mm, "end": v(20.46, 8.48) * mm});
            skLineSegment(sketch, "E782", {"start": v(20.46, 8.48) * mm, "end": v(20.33, 7.87) * mm});
            skLineSegment(sketch, "E783", {"start": v(20.33, 7.87) * mm, "end": v(20.39, 6.81) * mm});
            skLineSegment(sketch, "E784", {"start": v(20.39, 6.81) * mm, "end": v(20.5, 6.44) * mm});
            skLineSegment(sketch, "E785", {"start": v(20.5, 6.44) * mm, "end": v(20.6, 6.4) * mm});
            skLineSegment(sketch, "E786", {"start": v(20.6, 6.4) * mm, "end": v(20.56, 6.28) * mm});
            skLineSegment(sketch, "E787", {"start": v(20.56, 6.28) * mm, "end": v(20.57, 6.26) * mm});
            skLineSegment(sketch, "E788", {"start": v(20.57, 6.26) * mm, "end": v(21.39, 5.52) * mm});
            skLineSegment(sketch, "E789", {"start": v(21.39, 5.52) * mm, "end": v(21.52, 4.8) * mm});
            skLineSegment(sketch, "E790", {"start": v(21.52, 4.8) * mm, "end": v(19.96, 3.23) * mm});
            skLineSegment(sketch, "E791", {"start": v(19.96, 3.23) * mm, "end": v(19.23, 3.36) * mm});
            skLineSegment(sketch, "E792", {"start": v(19.23, 3.36) * mm, "end": v(18.49, 4.18) * mm});
            skLineSegment(sketch, "E793", {"start": v(18.49, 4.18) * mm, "end": v(18.47, 4.2) * mm});
            skLineSegment(sketch, "E794", {"start": v(18.47, 4.2) * mm, "end": v(18.36, 4.16) * mm});
            skLineSegment(sketch, "E795", {"start": v(18.36, 4.16) * mm, "end": v(18.32, 4.25) * mm});
            skLineSegment(sketch, "E796", {"start": v(18.32, 4.25) * mm, "end": v(17.94, 4.37) * mm});
            skLineSegment(sketch, "E797", {"start": v(17.94, 4.37) * mm, "end": v(16.88, 4.42) * mm});
            skLineSegment(sketch, "E798", {"start": v(16.88, 4.42) * mm, "end": v(16.28, 4.29) * mm});
            skCircle(sketch, "E799", {"center": v(-5.8, 0) * mm, "radius": 24.83 * mm, "construction": true});
            skCircle(sketch, "E800", {"center": v(24.76, 0) * mm, "radius": 1.15 * mm});
            skPoint(sketch, "E801.0.midPoint", {"position": v(-1.47, 2.5) * mm});
            skLineSegment(sketch, "E802", {"start": v(18.36, -4.17) * mm, "end": v(18.49, -4.2) * mm});
            skSolve(sketch);
        }
        {
            var Q0;
            Q0=makeQuery(id+"F0.imprint","IMPRINT",FACE,{"disambiguationData":[TD([[makeQuery(id+"F0.imprint","IMPRINT",EDGE,{"derivedFrom":sQuery(id+"F0.wireOp",EDGE,"E648")}),1.0]])]});
            extrude(context, id + "F1", {"entities" : qUnion([Q0]), "depth" : 5 * mm});
        }
    });
